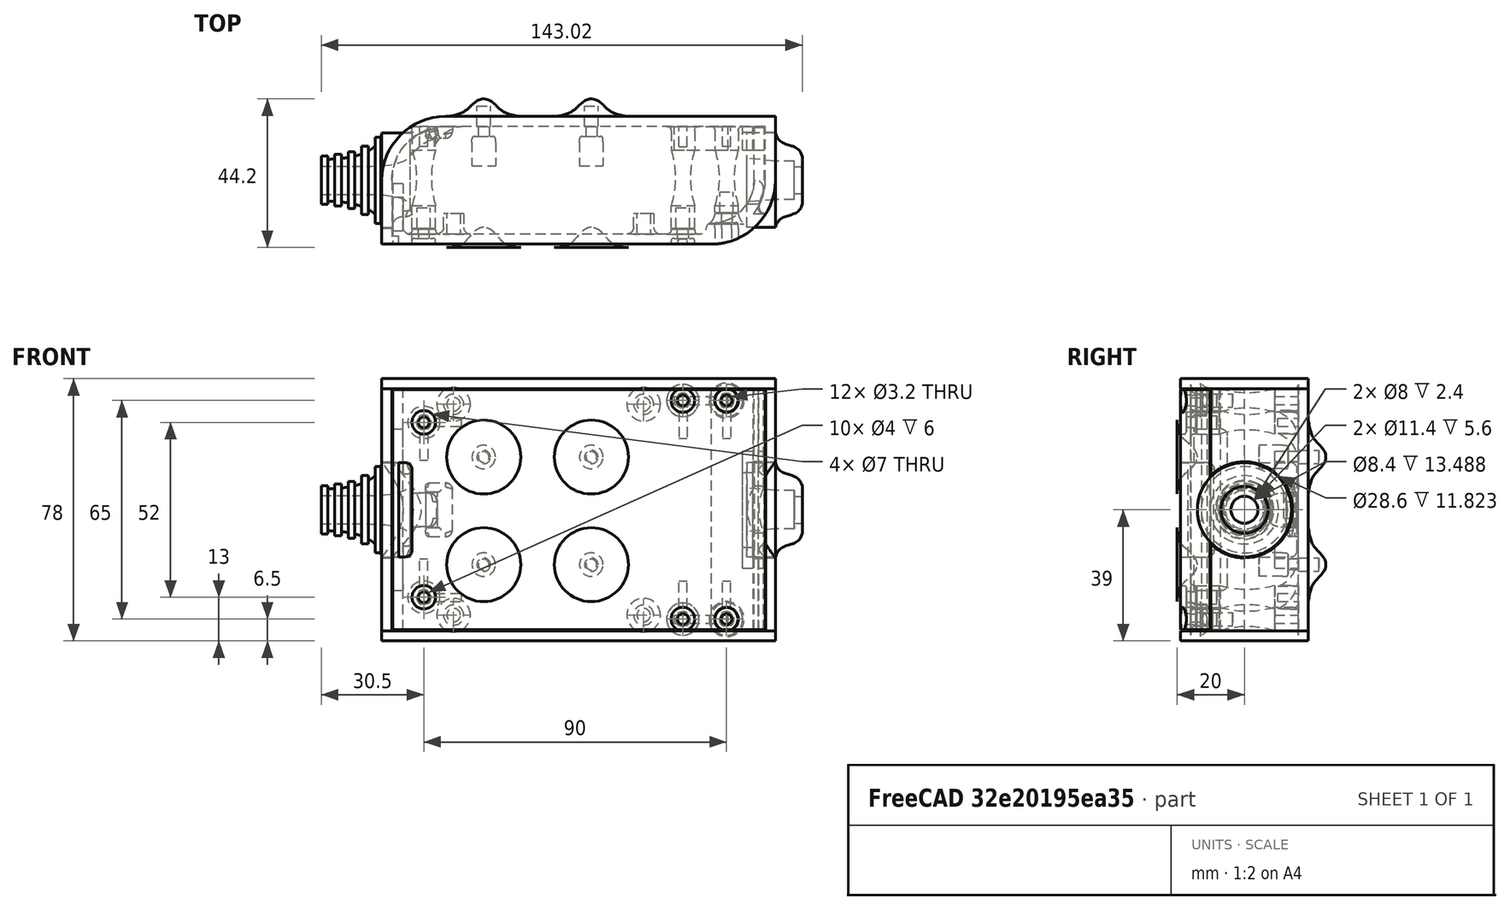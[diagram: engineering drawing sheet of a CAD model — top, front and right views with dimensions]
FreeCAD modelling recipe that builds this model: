
FCSTD DOCUMENT  (FreeCAD 0.19R0.19.2)
Label: enclosure_089
License: All rights reserved
LicenseURL: http://en.wikipedia.org/wiki/All_rights_reserved
objects: Part::Feature×68, Part::Revolution×68, Part::MultiFuse×50, Sketcher::SketchObject×28, Part::Fillet×22, Part::Cylinder×22, Part::Extrusion×18, Part::Cut×17, Part::Box×12, App::MeasureDistance×3
note: 305 computed .brp shape members not serialized (recipe doc carries the construction recipe); baked Part::Feature solids carry a one-line shape summary decoded from their .brp

FEATURE [Sketcher::SketchObject] Sketch  label="topSketch"
  FullyConstrained = true
  sketch-geometry (13):
    g0: LineSegment StartX=117 StartY=19 StartZ=0 EndX=117 EndY=38 EndZ=0
    g1: ArcOfCircle CenterX=98 CenterY=19 CenterZ=0 NormalX=0 NormalY=0 NormalZ=1 AngleXU=0 Radius=19 StartAngle=5.7297 EndAngle=6.28319
    g2: LineSegment StartX=0 StartY=3 StartZ=0 EndX=0 EndY=19 EndZ=0
    g3: LineSegment StartX=19 StartY=38 StartZ=0 EndX=117 EndY=38 EndZ=0
    g4: ArcOfCircle CenterX=19 CenterY=19 CenterZ=0 NormalX=0 NormalY=0 NormalZ=1 AngleXU=0 Radius=19 StartAngle=1.5708 EndAngle=3.14159
    g5: ArcOfCircle CenterX=19 CenterY=19 CenterZ=0 NormalX=0 NormalY=0 NormalZ=1 AngleXU=0 Radius=16 StartAngle=1.5708 EndAngle=3.14159
    g6: ArcOfCircle CenterX=98 CenterY=19 CenterZ=0 NormalX=0 NormalY=0 NormalZ=1 AngleXU=0 Radius=16 StartAngle=5.60905 EndAngle=6.28319
    g7: LineSegment StartX=114 StartY=19 StartZ=0 EndX=114 EndY=35 EndZ=0
    g8: LineSegment StartX=110.5 StartY=9.01251 StartZ=0 EndX=114.163 EndY=9.01251 EndZ=0
    g9: LineSegment StartX=114 StartY=35 StartZ=0 EndX=19 EndY=35 EndZ=0
    g10: LineSegment StartX=0 StartY=3 StartZ=0 EndX=0 EndY=0 EndZ=0
    g11: LineSegment StartX=3 StartY=0 StartZ=0 EndX=0 EndY=0 EndZ=0
    g12: LineSegment StartX=3 StartY=19 StartZ=0 EndX=3 EndY=0 EndZ=0
  constraints (33):
    c: Vertical(g0)
    c: Distance(g0) = 19
    c: Block(g0)
    c: Coincident(g1,g0)
    c: Block(g1)
    c: Vertical(g2)
    c: Block(g2)
    c: Coincident(g3,g0)
    c: Horizontal(g3)
    c: Distance(g3) = 98
    c: Coincident(g4,g3)
    c: Coincident(g4,g2)
    c: Block(g4)
    c: Coincident(g5,g4)
    c: Coincident(g6,g1)
    c: Block(g6)
    c: Block(g5)
    c: Coincident(g7,g6)
    c: Vertical(g7)
    c: Coincident(g8,g6)
    c: Coincident(g8,g1)
    c: Coincident(g9,g7)
    c: Coincident(g9,g5)
    c: Horizontal(g9)
    c: Tangent(g9,g5)
    c: Coincident(g10,g2)
    c: Distance(g10) = 3
    c: Vertical(g10)
    c: Coincident(g11,g10)
    c: Horizontal(g11)
    c: Coincident(g12,g5)
    c: Coincident(g12,g11)
    c: Vertical(g12)
FEATURE [Sketcher::SketchObject] Sketch001  label="bottomSketch"
  FullyConstrained = true
  sketch-geometry (32):
    g0: LineSegment StartX=3.3 StartY=-6.03275e-07 StartZ=0 EndX=98 EndY=-6.03275e-07 EndZ=0
    g1: ArcOfCircle CenterX=98 CenterY=19 CenterZ=0 NormalX=0 NormalY=0 NormalZ=1 AngleXU=0 Radius=19 StartAngle=4.71239 EndAngle=5.71103
    g2: LineSegment StartX=6.3 StartY=8 StartZ=0 EndX=3.3 EndY=8 EndZ=0
    g3: LineSegment StartX=3.3 StartY=8 StartZ=0 EndX=3.3 EndY=-6.03275e-07 EndZ=0
    g4: ArcOfCircle CenterX=8.3 CenterY=5 CenterZ=0 NormalX=0 NormalY=0 NormalZ=1 AngleXU=0 Radius=2 StartAngle=3.14159 EndAngle=4.71239
    g5: LineSegment StartX=6.3 StartY=8 StartZ=0 EndX=6.3 EndY=5 EndZ=0
    g6: ArcOfCircle CenterX=98 CenterY=19 CenterZ=0 NormalX=0 NormalY=0 NormalZ=1 AngleXU=0 Radius=12.7 StartAngle=4.71239 EndAngle=6.28319
    g7: LineSegment StartX=94.7 StartY=3 StartZ=0 EndX=8.3 EndY=3 EndZ=0
    g8-g12: Circle x5 (B-spline internal-alignment scaffolding for g13; pole/knot coordinates omitted)
    g13: BSplineCurve PolesCount=5 KnotsCount=3 Degree=3 IsPeriodic=0
    g14: GeomPoint X=98 Y=6.3 Z=0
    g15: GeomPoint X=96.3938 Y=4.71946 Z=0
    g16: GeomPoint X=94.7 Y=3 Z=0
    g17-g23: Circle x7 (B-spline internal-alignment scaffolding for g24; pole/knot coordinates omitted)
    g24: BSplineCurve PolesCount=7 KnotsCount=5 Degree=3 IsPeriodic=0
    g25-g29: GeomPoint x5 (B-spline internal-alignment scaffolding for g24; pole/knot coordinates omitted)
    g30: ArcOfCircle CenterX=98 CenterY=19 CenterZ=0 NormalX=0 NormalY=0 NormalZ=1 AngleXU=0 Radius=15.7 StartAngle=5.81226 EndAngle=6.28319
    g31: LineSegment StartX=110.7 StartY=19 StartZ=0 EndX=113.7 EndY=19 EndZ=0
  constraints (41):
    c: Horizontal(g0)
    c: Coincident(g1,g0)
    c: Block(g1)
    c: Horizontal(g2)
    c: Distance(g2) = 3
    c: Coincident(g3,g2)
    c: Vertical(g3)
    c: Coincident(g3,g0)
    c: Block(g4)
    c: Block(g2)
    c: Coincident(g5,g2)
    c: Coincident(g5,g4)
    c: Vertical(g5)
    c: Coincident(g6,g1)
    c: Block(g6)
    c: Coincident(g7,g4)
    c: Horizontal(g7)
    c: Block(g0)
    c: Block(g7)
    c: Block(g3)
    c: Coincident(g13,g6)
    c: Weight(g8) = 1
    c: Equal(g8, g9-g12) x4
    c: Coincident(g13,g7)
    c: InternalAlignment(g8-g12 -> g13) x5
    c: InternalAlignment(g14,g13)
    c: InternalAlignment(g15,g13)
    c: InternalAlignment(g16,g13)
    c: Block(g13)
    c: Weight(g17) = 1
    c: Equal(g17, g18-g23) x6
    c: Coincident(g24,g1)
    c: InternalAlignment(g17-g23 -> g24) x7
    c: InternalAlignment(g25-g29 -> g24) x5
    c: Block(g24)
    c: Coincident(g30,g24)
    c: Coincident(g31,g6)
    c: Coincident(g31,g30)
    c: Horizontal(g31)
    c: Block(g31)
    c: Block(g30)
FEATURE [Part::Extrusion] Extrude  label="top"
  Base = -> Sketch
  Dir = (0,0,1)
  DirMode = 2
  FaceMakerClass = Part::FaceMakerBullseye
  LengthFwd = 72
  LengthRev = 0
  Solid = true
  Symmetric = false
FEATURE [Part::Extrusion] Extrude001  label="bottom"
  Base = -> Sketch001
  Dir = (0,0,1)
  DirMode = 2
  FaceMakerClass = Part::FaceMakerBullseye
  LengthFwd = 71.4
  LengthRev = 0
  Placement = pos=(0,0,0.3) rot=(0,0,1;0rad)
  Solid = true
  Symmetric = false
FEATURE [Sketcher::SketchObject] Sketch002  label="topSketch001"
  FullyConstrained = true
  sketch-geometry (6):
    g0: LineSegment StartX=19 StartY=38 StartZ=0 EndX=117 EndY=38 EndZ=0
    g1: ArcOfCircle CenterX=19 CenterY=19 CenterZ=0 NormalX=0 NormalY=0 NormalZ=1 AngleXU=0 Radius=19 StartAngle=1.5708 EndAngle=3.14159
    g2: LineSegment StartX=117 StartY=38 StartZ=0 EndX=117 EndY=19 EndZ=0
    g3: LineSegment StartX=98 StartY=1.0161e-12 StartZ=0 EndX=5.22862e-06 EndY=1.0161e-12 EndZ=0
    g4: LineSegment StartX=5.22862e-06 StartY=19 StartZ=0 EndX=5.22862e-06 EndY=1.0161e-12 EndZ=0
    g5: ArcOfCircle CenterX=98 CenterY=19 CenterZ=0 NormalX=0 NormalY=0 NormalZ=1 AngleXU=0 Radius=19 StartAngle=4.71239 EndAngle=6.28319
  constraints (16):
    c: Horizontal(g0)
    c: Distance(g0) = 98
    c: Coincident(g1,g0)
    c: Block(g1)
    c: Coincident(g2,g0)
    c: Vertical(g2)
    c: Distance(g2) = 19
    c: Horizontal(g3)
    c: Coincident(g4,g1)
    c: Vertical(g4)
    c: Coincident(g3,g4)
    c: Block(g3)
    c: Coincident(g5,g2)
    c: Coincident(g5,g3)
    c: Block(g0)
    c: Block(g5)
FEATURE [Part::Extrusion] Extrude002  label="sideA"
  Base = -> Sketch002
  Dir = (0,0,1)
  DirMode = 2
  FaceMakerClass = Part::FaceMakerBullseye
  LengthFwd = 3
  LengthRev = 0
  Placement = pos=(0,0,-3) rot=(0,0,1;0rad)
  Solid = true
  Symmetric = false
FEATURE [Sketcher::SketchObject] Sketch003  label="topSketch002"
  FullyConstrained = true
  sketch-geometry (6):
    g0: LineSegment StartX=19 StartY=38 StartZ=0 EndX=117 EndY=38 EndZ=0
    g1: ArcOfCircle CenterX=19 CenterY=19 CenterZ=0 NormalX=0 NormalY=0 NormalZ=1 AngleXU=0 Radius=19 StartAngle=1.5708 EndAngle=3.14159
    g2: LineSegment StartX=117 StartY=38 StartZ=0 EndX=117 EndY=19 EndZ=0
    g3: LineSegment StartX=98 StartY=1.0161e-12 StartZ=0 EndX=5.22862e-06 EndY=1.0161e-12 EndZ=0
    g4: LineSegment StartX=5.22862e-06 StartY=19 StartZ=0 EndX=5.22862e-06 EndY=1.0161e-12 EndZ=0
    g5: ArcOfCircle CenterX=98 CenterY=19 CenterZ=0 NormalX=0 NormalY=0 NormalZ=1 AngleXU=0 Radius=19 StartAngle=4.71239 EndAngle=6.28319
  constraints (16):
    c: Horizontal(g0)
    c: Distance(g0) = 98
    c: Coincident(g1,g0)
    c: Block(g1)
    c: Coincident(g2,g0)
    c: Vertical(g2)
    c: Distance(g2) = 19
    c: Horizontal(g3)
    c: Coincident(g4,g1)
    c: Vertical(g4)
    c: Coincident(g3,g4)
    c: Block(g3)
    c: Coincident(g5,g2)
    c: Coincident(g5,g3)
    c: Block(g0)
    c: Block(g5)
FEATURE [Part::Extrusion] Extrude003  label="sideB"
  Base = -> Sketch003
  Dir = (0,0,1)
  DirMode = 2
  FaceMakerClass = Part::FaceMakerBullseye
  LengthFwd = 3
  LengthRev = 0
  Placement = pos=(0,0,72) rot=(0,0,1;0rad)
  Solid = true
  Symmetric = false
FEATURE [Sketcher::SketchObject] Sketch004
  FullyConstrained = true
  MapMode = 3
  Placement = pos=(0,0,0) rot=(1,0,0;1.5708rad)
  Support = -> [Extrude]
  sketch-geometry (8):
    g0: Circle CenterX=80.351 CenterY=-67.6202 CenterZ=0 NormalX=0 NormalY=0 NormalZ=1 AngleXU=0 Radius=2
    g1: Circle CenterX=80.351 CenterY=-67.6202 CenterZ=0 NormalX=0 NormalY=0 NormalZ=1 AngleXU=0 Radius=3
    g2: Circle CenterX=80.351 CenterY=-4.92017 CenterZ=0 NormalX=0 NormalY=0 NormalZ=1 AngleXU=0 Radius=2
    g3: Circle CenterX=80.351 CenterY=-4.92017 CenterZ=0 NormalX=0 NormalY=0 NormalZ=1 AngleXU=0 Radius=3
    g4: Circle CenterX=23.851 CenterY=-4.92017 CenterZ=0 NormalX=0 NormalY=0 NormalZ=1 AngleXU=0 Radius=2
    g5: Circle CenterX=23.851 CenterY=-4.92017 CenterZ=0 NormalX=0 NormalY=0 NormalZ=1 AngleXU=0 Radius=3
    g6: Circle CenterX=23.851 CenterY=-67.6202 CenterZ=0 NormalX=0 NormalY=0 NormalZ=1 AngleXU=0 Radius=2
    g7: Circle CenterX=23.851 CenterY=-67.6202 CenterZ=0 NormalX=0 NormalY=0 NormalZ=1 AngleXU=0 Radius=3
  constraints (8):
    c: Block(g3)
    c: Block(g2)
    c: Block(g1)
    c: Block(g0)
    c: Block(g6)
    c: Block(g7)
    c: Block(g4)
    c: Block(g5)
FEATURE [Part::Extrusion] Extrude004
  Base = -> Sketch004
  Dir = (0,-1,2e-16)
  DirMode = 2
  FaceMakerClass = Part::FaceMakerBullseye
  LengthFwd = 6
  LengthRev = 0
  Placement = pos=(0,9,0) rot=(0,0,1;0rad)
  Solid = true
  Symmetric = false
FEATURE [Sketcher::SketchObject] Sketch005
  FullyConstrained = true
  MapMode = 3
  Placement = pos=(0,0,0) rot=(1,0,0;1.5708rad)
  Support = -> [Extrude]
  sketch-geometry (8):
    g0: Circle CenterX=80.351 CenterY=-67.6202 CenterZ=0 NormalX=0 NormalY=0 NormalZ=1 AngleXU=0 Radius=3
    g1: Circle CenterX=80.351 CenterY=-4.92017 CenterZ=0 NormalX=0 NormalY=0 NormalZ=1 AngleXU=0 Radius=3
    g2: Circle CenterX=23.851 CenterY=-4.92017 CenterZ=0 NormalX=0 NormalY=0 NormalZ=1 AngleXU=0 Radius=3
    g3: Circle CenterX=23.851 CenterY=-67.6202 CenterZ=0 NormalX=0 NormalY=0 NormalZ=1 AngleXU=0 Radius=3
    g4: Circle CenterX=23.851 CenterY=-67.6202 CenterZ=0 NormalX=0 NormalY=0 NormalZ=1 AngleXU=0 Radius=5
    g5: Circle CenterX=80.351 CenterY=-67.6202 CenterZ=0 NormalX=0 NormalY=0 NormalZ=1 AngleXU=0 Radius=5
    g6: Circle CenterX=23.851 CenterY=-4.92017 CenterZ=0 NormalX=0 NormalY=0 NormalZ=1 AngleXU=0 Radius=5
    g7: Circle CenterX=80.351 CenterY=-4.92017 CenterZ=0 NormalX=0 NormalY=0 NormalZ=1 AngleXU=0 Radius=5
  constraints (8):
    c: Block(g1)
    c: Block(g0)
    c: Block(g3)
    c: Block(g2)
    c: Block(g5)
    c: Block(g4)
    c: Block(g6)
    c: Block(g7)
FEATURE [Part::Extrusion] Extrude005
  Base = -> Sketch005
  Dir = (0,-1,2e-16)
  DirMode = 2
  FaceMakerClass = Part::FaceMakerBullseye
  LengthFwd = 2
  LengthRev = 0
  Solid = true
  Symmetric = false
FEATURE [Sketcher::SketchObject] Sketch006
  FullyConstrained = true
  MapMode = 3
  Placement = pos=(0,0,0) rot=(1,0,0;1.5708rad)
  sketch-geometry (8):
    g0: Circle CenterX=80.351 CenterY=-67.6202 CenterZ=0 NormalX=0 NormalY=0 NormalZ=1 AngleXU=0 Radius=3
    g1: Circle CenterX=80.351 CenterY=-4.92017 CenterZ=0 NormalX=0 NormalY=0 NormalZ=1 AngleXU=0 Radius=3
    g2: Circle CenterX=23.851 CenterY=-4.92017 CenterZ=0 NormalX=0 NormalY=0 NormalZ=1 AngleXU=0 Radius=3
    g3: Circle CenterX=23.851 CenterY=-67.6202 CenterZ=0 NormalX=0 NormalY=0 NormalZ=1 AngleXU=0 Radius=3
    g4: Circle CenterX=23.851 CenterY=-67.6202 CenterZ=0 NormalX=0 NormalY=0 NormalZ=1 AngleXU=0 Radius=5
    g5: Circle CenterX=80.351 CenterY=-67.6202 CenterZ=0 NormalX=0 NormalY=0 NormalZ=1 AngleXU=0 Radius=5
    g6: Circle CenterX=23.851 CenterY=-4.92017 CenterZ=0 NormalX=0 NormalY=0 NormalZ=1 AngleXU=0 Radius=5
    g7: Circle CenterX=80.351 CenterY=-4.92017 CenterZ=0 NormalX=0 NormalY=0 NormalZ=1 AngleXU=0 Radius=5
  constraints (8):
    c: Block(g1)
    c: Block(g0)
    c: Block(g3)
    c: Block(g2)
    c: Block(g5)
    c: Block(g4)
    c: Block(g6)
    c: Block(g7)
FEATURE [Part::Extrusion] Extrude007
  Base = -> Sketch006
  Dir = (0,-1,2e-16)
  DirMode = 2
  FaceMakerClass = Part::FaceMakerBullseye
  LengthFwd = 2
  LengthRev = 0
  Solid = true
  Symmetric = false
FEATURE [Part::Fillet] Fillet
  Base = -> Extrude007
  Edges = 4 edges r=1.99: [Edge6,Edge12,Edge18,Edge24]
FEATURE [Part::Cut] Cut
  Base = -> Extrude005
  Placement = pos=(0,5,0) rot=(0,0,1;0rad)
  Tool = -> Fillet
FEATURE [Part::MultiFuse] Fusion  label="pCBScrews"
  Placement = pos=(-2.5,0,72.3) rot=(0,0,1;0rad)
  Shapes = -> [Extrude004,Cut]
FEATURE [App::MeasureDistance] Distance  label="Distance: 0.69 mm"
  Distance = 0.685967
  P1 = (24.0138,2.9647,0.3)
  P2 = (23.8901,3,-0.373787)
FEATURE [App::MeasureDistance] Distance001  label="Distance: 0.53 mm"
  Distance = 0.533607
  P1 = (80.2939,3,72.2334)
  P2 = (80.281,2.99661,71.7)
FEATURE [Part::Fillet] Fillet001
  Base = -> Extrude001
  Edges = 1 edges r=2.4: [Edge17]
FEATURE [Part::Fillet] Fillet002  label="bottom001"
  Base = -> Fillet001
  Edges = 1 edges r=2.4: [Edge36]
FEATURE [Part::Fillet] Fillet003  label="top001"
  Base = -> Extrude
  Edges = 1 edges r=2: [Edge1]
FEATURE [Sketcher::SketchObject] Sketch007
  FullyConstrained = true
  sketch-geometry (16):
    g0: LineSegment StartX=4 StartY=0 StartZ=0 EndX=4 EndY=2.4 EndZ=0
    g1: LineSegment StartX=4 StartY=2.4 StartZ=0 EndX=7 EndY=2.4 EndZ=0
    g2: LineSegment StartX=4 StartY=0 StartZ=0 EndX=5.7 EndY=0 EndZ=0
    g3: LineSegment StartX=5.7 StartY=0 StartZ=0 EndX=5.7 EndY=-5.6 EndZ=0
    g4-g8: Circle x5 (B-spline internal-alignment scaffolding for g9; pole/knot coordinates omitted)
    g9: BSplineCurve PolesCount=5 KnotsCount=3 Degree=3 IsPeriodic=0
    g10: GeomPoint X=7 Y=2.4 Z=0
    g11: GeomPoint X=10.4582 Y=-1.55472 Z=0
    g12: GeomPoint X=14 Y=-5.6 Z=0
    g13: LineSegment StartX=14 StartY=-5.6 StartZ=0 EndX=14 EndY=-14.1 EndZ=0
    g14: LineSegment StartX=14 StartY=-14.1 StartZ=0 EndX=6.5 EndY=-14.1 EndZ=0
    g15: LineSegment StartX=5.7 StartY=-5.6 StartZ=0 EndX=6.5 EndY=-14.1 EndZ=0
  constraints (28):
    c: Distance(g0) = 2.4
    c: Vertical(g0)
    c: Block(g0)
    c: Coincident(g1,g0)
    c: Horizontal(g1)
    c: Distance(g1) = 3
    c: Coincident(g2,g0)
    c: Horizontal(g2)
    c: Distance(g2) = 1.7
    c: Coincident(g3,g2)
    c: Vertical(g3)
    c: Distance(g3) = 5.6
    c: Coincident(g9,g1)
    c: Weight(g4) = 1
    c: Equal(g4, g5-g8) x4
    c: InternalAlignment(g4-g8 -> g9) x5
    c: InternalAlignment(g10,g9)
    c: InternalAlignment(g11,g9)
    c: InternalAlignment(g12,g9)
    c: Block(g9)
    c: Coincident(g13,g9)
    c: Vertical(g13)
    c: Distance(g13) = 8.5
    c: Coincident(g14,g13)
    c: Horizontal(g14)
    c: Distance(g14) = 7.5
    c: Coincident(g15,g3)
    c: Coincident(g15,g14)
FEATURE [Part::Feature] Face
  shape: bbox 10 x 16.5 x 2e-07 mm, 1 faces, 0 solids (baked)
FEATURE [Part::Revolution] Revolve  label="plugHousing"
  Angle = 360
  Axis = (0,1,0)
  Base = (0,0,0)
  FaceMakerClass = Part::FaceMakerBullseye
  Placement = pos=(0,0,36.15) rot=(0,0,1;0rad)
  Solid = false
  Source = -> Face
  Symmetric = false
FEATURE [Part::Feature] Face001
  shape: bbox 10 x 16.5 x 2e-07 mm, 1 faces, 0 solids (baked)
FEATURE [Part::Revolution] Revolve001  label="plugHousing001"
  Angle = 360
  Axis = (0,1,0)
  Base = (0,0,0)
  FaceMakerClass = Part::FaceMakerBullseye
  Placement = pos=(0,0,36.15) rot=(0,0,1;0rad)
  Solid = false
  Source = -> Face001
  Symmetric = false
FEATURE [Part::MultiFuse] Fusion001  label="plugHousing002"
  Placement = pos=(0,0,0) rot=(0,0,1;1.5708rad)
  Shapes = -> [Revolve001,Revolve]
FEATURE [Part::Feature] Face002
  shape: bbox 10 x 16.5 x 2e-07 mm, 1 faces, 0 solids (baked)
FEATURE [Part::Revolution] Revolve003  label="plugHousing005"
  Angle = 360
  Axis = (0,1,0)
  Base = (0,0,0)
  FaceMakerClass = Part::FaceMakerBullseye
  Placement = pos=(0,0,36.15) rot=(0,0,1;0rad)
  Solid = false
  Source = -> Face002
  Symmetric = false
FEATURE [Part::Feature] Face003
  shape: bbox 10 x 16.5 x 2e-07 mm, 1 faces, 0 solids (baked)
FEATURE [Part::Revolution] Revolve002  label="plugHousing003"
  Angle = 360
  Axis = (0,1,0)
  Base = (0,0,0)
  FaceMakerClass = Part::FaceMakerBullseye
  Placement = pos=(0,0,36.15) rot=(0,0,1;0rad)
  Solid = false
  Source = -> Face003
  Symmetric = false
FEATURE [Part::MultiFuse] Fusion002  label="plugHousing004"
  Placement = pos=(0,0,0) rot=(0,0,1;1.5708rad)
  Shapes = -> [Revolve002,Revolve003]
FEATURE [Part::MultiFuse] Fusion003  label="plugHousing006"
  Placement = pos=(0,19,0) rot=(0,0,1;3.14159rad)
  Shapes = -> [Fusion002,Fusion001]
FEATURE [Part::Feature] Face004
  shape: bbox 10 x 16.5 x 2e-07 mm, 1 faces, 0 solids (baked)
FEATURE [Part::Revolution] Revolve006  label="plugHousing010"
  Angle = 360
  Axis = (0,1,0)
  Base = (0,0,0)
  FaceMakerClass = Part::FaceMakerBullseye
  Placement = pos=(0,0,36.15) rot=(0,0,1;0rad)
  Solid = false
  Source = -> Face004
  Symmetric = false
FEATURE [Part::Feature] Face005
  shape: bbox 10 x 16.5 x 2e-07 mm, 1 faces, 0 solids (baked)
FEATURE [Part::Revolution] Revolve007  label="plugHousing011"
  Angle = 360
  Axis = (0,1,0)
  Base = (0,0,0)
  FaceMakerClass = Part::FaceMakerBullseye
  Placement = pos=(0,0,36.15) rot=(0,0,1;0rad)
  Solid = false
  Source = -> Face005
  Symmetric = false
FEATURE [Part::Feature] Face006
  shape: bbox 10 x 16.5 x 2e-07 mm, 1 faces, 0 solids (baked)
FEATURE [Part::Revolution] Revolve004  label="plugHousing007"
  Angle = 360
  Axis = (0,1,0)
  Base = (0,0,0)
  FaceMakerClass = Part::FaceMakerBullseye
  Placement = pos=(0,0,36.15) rot=(0,0,1;0rad)
  Solid = false
  Source = -> Face006
  Symmetric = false
FEATURE [Part::MultiFuse] Fusion004  label="plugHousing009"
  Placement = pos=(0,0,0) rot=(0,0,1;1.5708rad)
  Shapes = -> [Revolve004,Revolve007]
FEATURE [Part::Feature] Face007
  shape: bbox 10 x 16.5 x 2e-07 mm, 1 faces, 0 solids (baked)
FEATURE [Part::Revolution] Revolve005  label="plugHousing008"
  Angle = 360
  Axis = (0,1,0)
  Base = (0,0,0)
  FaceMakerClass = Part::FaceMakerBullseye
  Placement = pos=(0,0,36.15) rot=(0,0,1;0rad)
  Solid = false
  Source = -> Face007
  Symmetric = false
FEATURE [Part::MultiFuse] Fusion005  label="plugHousing012"
  Placement = pos=(0,0,0) rot=(0,0,1;1.5708rad)
  Shapes = -> [Revolve006,Revolve005]
FEATURE [Part::MultiFuse] Fusion006  label="plugHousing013"
  Placement = pos=(0,19,0) rot=(0,0,1;3.14159rad)
  Shapes = -> [Fusion005,Fusion004]
FEATURE [Part::MultiFuse] Fusion007  label="plugHousing014"
  Placement = pos=(122.621,0,-0.15) rot=(0,0,1;0rad)
  Shapes = -> [Fusion003,Fusion006]
FEATURE [Part::Cylinder] Cylinder002
  Angle = 360
  AttacherType = Attacher::AttachEngine3D
  Height = 20
  Placement = pos=(0,0,36.15) rot=(0,0,1;0rad)
  Radius = 4
FEATURE [Part::Cylinder] Cylinder003
  Angle = 360
  AttacherType = Attacher::AttachEngine3D
  Height = 10
  Placement = pos=(0,0,36.15) rot=(0,0,1;0rad)
  Radius = 4
FEATURE [Part::MultiFuse] Fusion009  label="removeToCreateHoleForPlugHousing"
  Placement = pos=(70,19,36.15) rot=(0,1,0;1.5708rad)
  Shapes = -> [Cylinder002,Cylinder003]
FEATURE [Part::Cylinder] Cylinder004
  Angle = 360
  AttacherType = Attacher::AttachEngine3D
  Height = 20
  Placement = pos=(0,0,36.15) rot=(0,0,1;0rad)
  Radius = 4
FEATURE [Part::Cylinder] Cylinder005
  Angle = 360
  AttacherType = Attacher::AttachEngine3D
  Height = 10
  Placement = pos=(0,0,36.15) rot=(0,0,1;0rad)
  Radius = 4
FEATURE [Part::MultiFuse] Fusion010  label="removeToCreateHoleForPlugHousing001"
  Placement = pos=(70,19,36.15) rot=(0,1,0;1.5708rad)
  Shapes = -> [Cylinder004,Cylinder005]
FEATURE [Part::Cut] Cut001
  Base = -> Fillet003
  Tool = -> Fusion010
FEATURE [Part::Cut] Cut002  label="Bottom"
  Base = -> Fillet002
  Tool = -> Fusion009
FEATURE [Part::Feature] Face008
  shape: bbox 10 x 16.5 x 2e-07 mm, 1 faces, 0 solids (baked)
FEATURE [Part::Revolution] Revolve011  label="plugHousing021"
  Angle = 360
  Axis = (0,1,0)
  Base = (0,0,0)
  FaceMakerClass = Part::FaceMakerBullseye
  Placement = pos=(0,0,36.15) rot=(0,0,1;0rad)
  Solid = false
  Source = -> Face008
  Symmetric = false
FEATURE [Part::Feature] Face009
  shape: bbox 10 x 16.5 x 2e-07 mm, 1 faces, 0 solids (baked)
FEATURE [Part::Revolution] Revolve012  label="plugHousing022"
  Angle = 360
  Axis = (0,1,0)
  Base = (0,0,0)
  FaceMakerClass = Part::FaceMakerBullseye
  Placement = pos=(0,0,36.15) rot=(0,0,1;0rad)
  Solid = false
  Source = -> Face009
  Symmetric = false
FEATURE [Part::Feature] Face010 .. Face013  x4 (patterned run collapsed; names and placements below)
  shape: bbox 10 x 16.5 x 2e-07 mm, 1 faces, 0 solids (baked)
FEATURE [Part::Revolution] Revolve015  label="plugHousing027"
  Angle = 360
  Axis = (0,1,0)
  Base = (0,0,0)
  FaceMakerClass = Part::FaceMakerBullseye
  Placement = pos=(0,0,36.15) rot=(0,0,1;0rad)
  Solid = false
  Source = -> Face013
  Symmetric = false
FEATURE [Part::Feature] Face014
  shape: bbox 10 x 16.5 x 2e-07 mm, 1 faces, 0 solids (baked)
FEATURE [Part::Feature] Face015
  shape: bbox 10 x 16.5 x 2e-07 mm, 1 faces, 0 solids (baked)
FEATURE [Part::Feature] Face016
  shape: bbox 10 x 16.5 x 2e-07 mm, 1 faces, 0 solids (baked)
FEATURE [Part::Revolution] Revolve019  label="plugHousing033"
  Angle = 360
  Axis = (0,1,0)
  Base = (0,0,0)
  FaceMakerClass = Part::FaceMakerBullseye
  Placement = pos=(0,0,36.15) rot=(0,0,1;0rad)
  Solid = false
  Source = -> Face016
  Symmetric = false
FEATURE [Part::Feature] Face017
  shape: bbox 10 x 16.5 x 2e-07 mm, 1 faces, 0 solids (baked)
FEATURE [Part::Revolution] Revolve020  label="plugHousing034"
  Angle = 360
  Axis = (0,1,0)
  Base = (0,0,0)
  FaceMakerClass = Part::FaceMakerBullseye
  Placement = pos=(0,0,36.15) rot=(0,0,1;0rad)
  Solid = false
  Source = -> Face017
  Symmetric = false
FEATURE [Part::Feature] Face018
  shape: bbox 10 x 16.5 x 2e-07 mm, 1 faces, 0 solids (baked)
FEATURE [Part::Revolution] Revolve016  label="plugHousing030"
  Angle = 360
  Axis = (0,1,0)
  Base = (0,0,0)
  FaceMakerClass = Part::FaceMakerBullseye
  Placement = pos=(0,0,36.15) rot=(0,0,1;0rad)
  Solid = false
  Source = -> Face018
  Symmetric = false
FEATURE [Part::MultiFuse] Fusion020  label="plugHousing038"
  Placement = pos=(0,0,0) rot=(0,0,1;1.5708rad)
  Shapes = -> [Revolve016,Revolve020]
FEATURE [Part::Feature] Face019
  shape: bbox 10 x 16.5 x 2e-07 mm, 1 faces, 0 solids (baked)
FEATURE [Part::Feature] Face020
  shape: bbox 10 x 16.5 x 2e-07 mm, 1 faces, 0 solids (baked)
FEATURE [Part::Revolution] Revolve017  label="plugHousing031"
  Angle = 360
  Axis = (0,1,0)
  Base = (0,0,0)
  FaceMakerClass = Part::FaceMakerBullseye
  Placement = pos=(0,0,36.15) rot=(0,0,1;0rad)
  Solid = false
  Source = -> Face020
  Symmetric = false
FEATURE [Part::MultiFuse] Fusion021  label="plugHousing039"
  Placement = pos=(0,0,0) rot=(0,0,1;1.5708rad)
  Shapes = -> [Revolve019,Revolve017]
FEATURE [Part::MultiFuse] Fusion023  label="plugHousing041"
  Placement = pos=(0,19,0) rot=(0,0,1;3.14159rad)
  Shapes = -> [Fusion021,Fusion020]
FEATURE [Part::Revolution] Revolve022  label="plugHousing043"
  Angle = 360
  Axis = (0,1,0)
  Base = (0,0,0)
  FaceMakerClass = Part::FaceMakerBullseye
  Placement = pos=(0,0,36.15) rot=(0,0,1;0rad)
  Solid = false
  Source = -> Face019
  Symmetric = false
FEATURE [Part::Feature] Face021
  shape: bbox 10 x 16.5 x 2e-07 mm, 1 faces, 0 solids (baked)
FEATURE [Part::Revolution] Revolve023  label="plugHousing044"
  Angle = 360
  Axis = (0,1,0)
  Base = (0,0,0)
  FaceMakerClass = Part::FaceMakerBullseye
  Placement = pos=(0,0,36.15) rot=(0,0,1;0rad)
  Solid = false
  Source = -> Face021
  Symmetric = false
FEATURE [Part::Feature] Face022
  shape: bbox 10 x 16.5 x 2e-07 mm, 1 faces, 0 solids (baked)
FEATURE [Part::Revolution] Revolve018  label="plugHousing032"
  Angle = 360
  Axis = (0,1,0)
  Base = (0,0,0)
  FaceMakerClass = Part::FaceMakerBullseye
  Placement = pos=(0,0,36.15) rot=(0,0,1;0rad)
  Solid = false
  Source = -> Face022
  Symmetric = false
FEATURE [Part::MultiFuse] Fusion022  label="plugHousing040"
  Placement = pos=(0,0,0) rot=(0,0,1;1.5708rad)
  Shapes = -> [Revolve018,Revolve023]
FEATURE [Part::Feature] Face023
  shape: bbox 10 x 16.5 x 2e-07 mm, 1 faces, 0 solids (baked)
FEATURE [Part::Revolution] Revolve021  label="plugHousing035"
  Angle = 360
  Axis = (0,1,0)
  Base = (0,0,0)
  FaceMakerClass = Part::FaceMakerBullseye
  Placement = pos=(0,0,36.15) rot=(0,0,1;0rad)
  Solid = false
  Source = -> Face023
  Symmetric = false
FEATURE [Part::MultiFuse] Fusion018  label="plugHousing036"
  Placement = pos=(0,0,0) rot=(0,0,1;1.5708rad)
  Shapes = -> [Revolve022,Revolve021]
FEATURE [Part::MultiFuse] Fusion019  label="plugHousing037"
  Placement = pos=(0,19,0) rot=(0,0,1;3.14159rad)
  Shapes = -> [Fusion018,Fusion022]
FEATURE [Part::MultiFuse] Fusion024  label="plugHousing042"
  Placement = pos=(122.621,0,-0.15) rot=(0,0,1;0rad)
  Shapes = -> [Fusion023,Fusion019]
FEATURE [Part::Cylinder] Cylinder006
  Angle = 360
  AttacherType = Attacher::AttachEngine3D
  Height = 20
  Placement = pos=(0,0,36.15) rot=(0,0,1;0rad)
  Radius = 14.3
FEATURE [Part::Cylinder] Cylinder007
  Angle = 360
  AttacherType = Attacher::AttachEngine3D
  Height = 10
  Placement = pos=(0,0,36.15) rot=(0,0,1;0rad)
  Radius = 4
FEATURE [Part::MultiFuse] Fusion026  label="removeToCreteHoleForPlugHousing"
  Placement = pos=(70,19,36) rot=(0,1,0;1.5708rad)
  Shapes = -> [Cylinder006,Cylinder007]
FEATURE [Part::Box] Box001  label="Cube001"
  AttacherType = Attacher::AttachEngine3D
  Height = 28
  Length = 3
  Placement = pos=(110.7,19,22) rot=(0,0,1;0rad)
  Width = 15.7
FEATURE [Part::Cut] Cut003  label="top002"
  Base = -> Cut001
  Tool = -> Fusion007
FEATURE [Part::Revolution] Revolve008  label="plugHousing015"
  Angle = 360
  Axis = (0,1,0)
  Base = (0,0,0)
  FaceMakerClass = Part::FaceMakerBullseye
  Placement = pos=(0,0,36.15) rot=(0,0,1;0rad)
  Solid = false
  Source = -> Face010
  Symmetric = false
FEATURE [Part::MultiFuse] Fusion013  label="plugHousing020"
  Placement = pos=(0,0,0) rot=(0,0,1;1.5708rad)
  Shapes = -> [Revolve008,Revolve012]
FEATURE [Part::Cut] Cut004  label="top003"
  Base = -> Cut003
  Placement = pos=(1,0,0) rot=(0,0,1;0rad)
  Tool = -> Fusion026
FEATURE [Part::Cylinder] Cylinder008
  Angle = 360
  AttacherType = Attacher::AttachEngine3D
  Height = 20
  Placement = pos=(0,0,36.15) rot=(0,0,1;0rad)
  Radius = 10.3
FEATURE [Part::Cylinder] Cylinder009
  Angle = 360
  AttacherType = Attacher::AttachEngine3D
  Height = 10
  Placement = pos=(0,0,36.15) rot=(0,0,1;0rad)
  Radius = 4
FEATURE [Part::MultiFuse] Fusion027  label="removeToCreteHoleForPlugHousing001"
  Placement = pos=(70,19,36) rot=(0,1,0;1.5708rad)
  Shapes = -> [Cylinder008,Cylinder009]
FEATURE [Part::Cut] Cut005  label="plugHousingTab"
  Base = -> Box001
  Tool = -> Fusion027
FEATURE [Part::MultiFuse] Fusion028  label="plugHousing045"
  Shapes = -> [Fusion024,Cut005]
FEATURE [Part::Box] Box002  label="Cube002"
  AttacherType = Attacher::AttachEngine3D
  Height = 28.8
  Length = 3
  Placement = pos=(107.3,28,21.6) rot=(0,0,1;0rad)
  Width = 7
FEATURE [Part::Box] Box003  label="Cube003"
  AttacherType = Attacher::AttachEngine3D
  Height = 3
  Length = 6.4
  Placement = pos=(107.3,28,18.6) rot=(0,0,1;0rad)
  Width = 7
FEATURE [Part::Box] Box004  label="Cube004"
  AttacherType = Attacher::AttachEngine3D
  Height = 3
  Length = 6.4
  Placement = pos=(107.3,28,50.4) rot=(0,0,1;0rad)
  Width = 7
FEATURE [Part::MultiFuse] Fusion029  label="plugHousingBracketHolder"
  Shapes = -> [Box004,Box002,Box003]
FEATURE [Part::Cylinder] Cylinder010
  Angle = 360
  AttacherType = Attacher::AttachEngine3D
  Height = 20
  Placement = pos=(0,0,36.15) rot=(0,0,1;0rad)
  Radius = 14.3
FEATURE [Part::Cylinder] Cylinder011
  Angle = 360
  AttacherType = Attacher::AttachEngine3D
  Height = 10
  Placement = pos=(0,0,36.15) rot=(0,0,1;0rad)
  Radius = 4
FEATURE [Part::MultiFuse] Fusion030  label="removeToCreteHoleForPlugHousing002"
  Placement = pos=(70,19,36) rot=(0,1,0;1.5708rad)
  Shapes = -> [Cylinder010,Cylinder011]
FEATURE [Part::Cut] Cut006  label="plugHousingBracketHolder001"
  Base = -> Fusion029
  Tool = -> Fusion030
FEATURE [Part::Cylinder] Cylinder012
  Angle = 360
  AttacherType = Attacher::AttachEngine3D
  Height = 20
  Placement = pos=(0,0,36.15) rot=(0,0,1;0rad)
  Radius = 7
FEATURE [Part::Cylinder] Cylinder013
  Angle = 360
  AttacherType = Attacher::AttachEngine3D
  Height = 10
  Placement = pos=(0,0,36.15) rot=(0,0,1;0rad)
  Radius = 4
FEATURE [Part::MultiFuse] Fusion032  label="removeToCreteHoleForPlugHousing003"
  Placement = pos=(70,19,36) rot=(0,1,0;1.5708rad)
  Shapes = -> [Cylinder012,Cylinder013]
FEATURE [Part::Cut] Cut007  label="bottom002"
  Base = -> Cut002
  Tool = -> Fusion032
FEATURE [Sketcher::SketchObject] Sketch008
  FullyConstrained = true
  sketch-geometry (54):
    g0: LineSegment StartX=-4.2 StartY=0 StartZ=0 EndX=-6.2 EndY=0 EndZ=0
    g1: LineSegment StartX=-14 StartY=-18 StartZ=0 EndX=-14 EndY=-26.5 EndZ=0
    g2: LineSegment StartX=-4.2 StartY=0 StartZ=0 EndX=-4.2 EndY=-13.4877 EndZ=0
    g3: Circle CenterX=-4.2 CenterY=-13.4877 CenterZ=0 NormalX=0 NormalY=0 NormalZ=1 AngleXU=0 Radius=1
    g4: Circle CenterX=-4.2 CenterY=-26.5 CenterZ=0 NormalX=0 NormalY=0 NormalZ=1 AngleXU=0 Radius=1
    g5: Circle CenterX=-8.2 CenterY=-26.5 CenterZ=0 NormalX=0 NormalY=0 NormalZ=1 AngleXU=0 Radius=1
    g6: BSplineCurve PolesCount=3 KnotsCount=2 Degree=2 IsPeriodic=0
    g7: GeomPoint X=-4.2 Y=-13.4877 Z=0
    g8: GeomPoint X=-8.2 Y=-26.5 Z=0
    g9: LineSegment StartX=-14 StartY=-26.5 StartZ=0 EndX=-8.2 EndY=-26.5 EndZ=0
    g10: LineSegment StartX=-10.15 StartY=-12 StartZ=0 EndX=-10.15 EndY=-14 EndZ=0
    g11: LineSegment StartX=-12.8401 StartY=-16 StartZ=0 EndX=-10.1571 EndY=-16 EndZ=0
    g12: LineSegment StartX=-10.15 StartY=-14 StartZ=0 EndX=-8.70761 EndY=-14 EndZ=0
    g13: LineSegment StartX=-12.8401 StartY=-16 StartZ=0 EndX=-12.8401 EndY=-17.6958 EndZ=0
    g14: LineSegment StartX=-10.15 StartY=-12 StartZ=0 EndX=-7.79258 EndY=-12 EndZ=0
    g15: Circle CenterX=-6.2215 CenterY=-2 CenterZ=0 NormalX=0 NormalY=0 NormalZ=1 AngleXU=0 Radius=1
    g16: Circle CenterX=-6.22762 CenterY=-2.58724 CenterZ=0 NormalX=0 NormalY=0 NormalZ=1 AngleXU=0 Radius=1
    g17: Circle CenterX=-6.32538 CenterY=-4 CenterZ=0 NormalX=0 NormalY=0 NormalZ=1 AngleXU=0 Radius=1
    g18: BSplineCurve PolesCount=3 KnotsCount=2 Degree=2 IsPeriodic=0
    g19: GeomPoint X=-6.2215 Y=-2 Z=0
    g20: GeomPoint X=-6.32538 Y=-4 Z=0
    g21: Circle CenterX=-6.48644 CenterY=-5.99526 CenterZ=0 NormalX=0 NormalY=0 NormalZ=1 AngleXU=0 Radius=1
    g22: Circle CenterX=-6.58486 CenterY=-6.99526 CenterZ=0 NormalX=0 NormalY=0 NormalZ=1 AngleXU=0 Radius=1
    g23: Circle CenterX=-6.77343 CenterY=-8 CenterZ=0 NormalX=0 NormalY=0 NormalZ=1 AngleXU=0 Radius=1
    g24: BSplineCurve PolesCount=3 KnotsCount=2 Degree=2 IsPeriodic=0
    g25: GeomPoint X=-6.48644 Y=-5.99526 Z=0
    g26: GeomPoint X=-6.77343 Y=-8 Z=0
    g27: Circle CenterX=-7.19003 CenterY=-10 CenterZ=0 NormalX=0 NormalY=0 NormalZ=1 AngleXU=0 Radius=1
    g28: Circle CenterX=-7.44407 CenterY=-11.0915 CenterZ=0 NormalX=0 NormalY=0 NormalZ=1 AngleXU=0 Radius=1
    g29: Circle CenterX=-7.79258 CenterY=-12 CenterZ=0 NormalX=0 NormalY=0 NormalZ=1 AngleXU=0 Radius=1
    g30: BSplineCurve PolesCount=3 KnotsCount=2 Degree=2 IsPeriodic=0
    g31: GeomPoint X=-7.19003 Y=-10 Z=0
    g32: GeomPoint X=-7.79258 Y=-12 Z=0
    g33: Circle CenterX=-8.70761 CenterY=-14 CenterZ=0 NormalX=0 NormalY=0 NormalZ=1 AngleXU=0 Radius=1
    g34: Circle CenterX=-9.33087 CenterY=-15.1837 CenterZ=0 NormalX=0 NormalY=0 NormalZ=1 AngleXU=0 Radius=1
    g35: Circle CenterX=-10.1571 CenterY=-16 CenterZ=0 NormalX=0 NormalY=0 NormalZ=1 AngleXU=0 Radius=1
    g36: BSplineCurve PolesCount=3 KnotsCount=2 Degree=2 IsPeriodic=0
    g37: GeomPoint X=-8.70761 Y=-14 Z=0
    g38: GeomPoint X=-10.1571 Y=-16 Z=0
    g39: Circle CenterX=-12.8401 CenterY=-17.6958 CenterZ=0 NormalX=0 NormalY=0 NormalZ=1 AngleXU=0 Radius=1
    g40: Circle CenterX=-13.3521 CenterY=-17.9027 CenterZ=0 NormalX=0 NormalY=0 NormalZ=1 AngleXU=0 Radius=1
    g41: Circle CenterX=-14 CenterY=-18 CenterZ=0 NormalX=0 NormalY=0 NormalZ=1 AngleXU=0 Radius=1
    g42: BSplineCurve PolesCount=3 KnotsCount=2 Degree=2 IsPeriodic=0
    g43: GeomPoint X=-12.8401 Y=-17.6958 Z=0
    g44: GeomPoint X=-14 Y=-18 Z=0
    g45: LineSegment StartX=-6.2 StartY=0 StartZ=0 EndX=-7.2 EndY=0 EndZ=0
    g46: LineSegment StartX=-7.2 StartY=0 StartZ=0 EndX=-7.2 EndY=-2 EndZ=0
    g47: LineSegment StartX=-7.2 StartY=-2 StartZ=0 EndX=-6.2215 EndY=-2 EndZ=0
    g48: LineSegment StartX=-6.32538 StartY=-4 StartZ=0 EndX=-7.65538 EndY=-4 EndZ=0
    g49: LineSegment StartX=-7.65538 StartY=-4 StartZ=0 EndX=-7.65538 EndY=-5.99526 EndZ=0
    g50: LineSegment StartX=-7.65538 StartY=-5.99526 StartZ=0 EndX=-6.48644 EndY=-5.99526 EndZ=0
    g51: LineSegment StartX=-6.77343 StartY=-8 StartZ=0 EndX=-8.43343 EndY=-8 EndZ=0
    g52: LineSegment StartX=-8.43343 StartY=-8 StartZ=0 EndX=-8.43343 EndY=-10 EndZ=0
    g53: LineSegment StartX=-8.43343 StartY=-10 StartZ=0 EndX=-7.19003 EndY=-10 EndZ=0
  constraints (112):
    c: Horizontal(g0)
    c: Distance(g0) = 2
    c: Block(g0)
    c: Vertical(g1)
    c: Coincident(g2,g0)
    c: Vertical(g2)
    c: Block(g2)
    c: Coincident(g6,g2)
    c: Weight(g3) = 1
    c: Equal(g3,g4)
    c: Equal(g3,g5)
    c: InternalAlignment(g3,g6)
    c: InternalAlignment(g4,g6)
    c: InternalAlignment(g5,g6)
    c: InternalAlignment(g7,g6)
    c: InternalAlignment(g8,g6)
    c: Block(g6)
    c: Coincident(g9,g1)
    c: Coincident(g9,g6)
    c: Horizontal(g9)
    c: Vertical(g10)
    c: Block(g10)
    c: Horizontal(g11)
    c: Block(g11)
    c: Coincident(g12,g10)
    c: Horizontal(g12)
    c: Block(g12)
    c: Coincident(g13,g11)
    c: Vertical(g13)
    c: Block(g13)
    c: Coincident(g14,g10)
    c: Horizontal(g14)
    c: Block(g14)
    c: Block(g9)
    c: Block(g1)
    c: Weight(g15) = 1
    c: Equal(g15,g16)
    c: Equal(g15,g17)
    c: InternalAlignment(g15,g18)
    c: InternalAlignment(g16,g18)
    c: InternalAlignment(g17,g18)
    c: InternalAlignment(g19,g18)
    c: InternalAlignment(g20,g18)
    c: Weight(g21) = 1
    c: Equal(g21,g22)
    c: Equal(g21,g23)
    c: InternalAlignment(g21,g24)
    c: InternalAlignment(g22,g24)
    c: InternalAlignment(g23,g24)
    c: InternalAlignment(g25,g24)
    c: InternalAlignment(g26,g24)
    c: Weight(g27) = 1
    c: Equal(g27,g28)
    c: Equal(g27,g29)
    c: Coincident(g30,g14)
    c: InternalAlignment(g27,g30)
    c: InternalAlignment(g28,g30)
    c: InternalAlignment(g29,g30)
    c: InternalAlignment(g31,g30)
    c: InternalAlignment(g32,g30)
    c: Coincident(g36,g12)
    c: Weight(g33) = 1
    c: Equal(g33,g34)
    c: Equal(g33,g35)
    c: Coincident(g36,g11)
    c: InternalAlignment(g33,g36)
    c: InternalAlignment(g34,g36)
    c: InternalAlignment(g35,g36)
    c: InternalAlignment(g37,g36)
    c: InternalAlignment(g38,g36)
    c: Coincident(g42,g13)
    c: Weight(g39) = 1
    c: Equal(g39,g40)
    c: Equal(g39,g41)
    c: Coincident(g42,g1)
    c: InternalAlignment(g39,g42)
    c: InternalAlignment(g40,g42)
    c: InternalAlignment(g41,g42)
    c: InternalAlignment(g43,g42)
    c: InternalAlignment(g44,g42)
    c: Block(g18)
    c: Block(g24)
    c: Block(g30)
    c: Block(g36)
    c: Block(g42)
    c: Horizontal(g45)
    c: Coincident(g45,g0)
    c: Vertical(g46)
    c: Coincident(g46,g45)
    c: Coincident(g47,g46)
    c: Coincident(g47,g18)
    c: Horizontal(g47)
    c: Block(g46)
    c: Coincident(g48,g18)
    c: Horizontal(g48)
    c: Distance(g48) = 1.33
    c: Vertical(g49)
    c: Coincident(g49,g48)
    c: Coincident(g50,g49)
    c: Coincident(g50,g24)
    c: Horizontal(g50)
    c: Tangent(g50,g22)
    c: Horizontal(g51)
    c: Coincident(g51,g24)
    c: Block(g51)
    c: Vertical(g52)
    c: Block(g52)
    c: Coincident(g52,g51)
    c: Coincident(g53,g52)
    c: Coincident(g53,g30)
    c: Horizontal(g53)
    c: Distance(g1) = 8.5
FEATURE [Part::Feature] Face024
  shape: bbox 9.8 x 26.5 x 2e-07 mm, 1 faces, 0 solids (baked)
FEATURE [Part::Revolution] Revolve024
  Angle = 360
  Axis = (0,1,0)
  Base = (0,0,0)
  FaceMakerClass = Part::FaceMakerBullseye
  Placement = pos=(0,0,0) rot=(0,0,1;1.5708rad)
  Solid = false
  Source = -> Face024
  Symmetric = false
FEATURE [Part::Feature] Face025
  shape: bbox 9.8 x 26.5 x 2e-07 mm, 1 faces, 0 solids (baked)
FEATURE [Part::Revolution] Revolve025
  Angle = 360
  Axis = (0,1,0)
  Base = (0,0,0)
  FaceMakerClass = Part::FaceMakerBullseye
  Placement = pos=(0,0,0) rot=(0,0,1;1.5708rad)
  Solid = false
  Source = -> Face025
  Symmetric = false
FEATURE [Part::MultiFuse] Fusion033
  Placement = pos=(-18,19,36) rot=(0,0,1;0rad)
  Shapes = -> [Revolve025,Revolve024]
FEATURE [Part::Cylinder] Cylinder014
  Angle = 360
  AttacherType = Attacher::AttachEngine3D
  Height = 20
  Placement = pos=(0,0,36.15) rot=(0,0,1;0rad)
  Radius = 14.3
FEATURE [Part::Cylinder] Cylinder015
  Angle = 360
  AttacherType = Attacher::AttachEngine3D
  Height = 10
  Placement = pos=(0,0,36.15) rot=(0,0,1;0rad)
  Radius = 4
FEATURE [Part::MultiFuse] Fusion034  label="removeToCreteHoleForPlugHousing004"
  Placement = pos=(-42,19,36) rot=(0,1,0;1.5708rad)
  Shapes = -> [Cylinder014,Cylinder015]
FEATURE [Part::Cut] Cut008  label="top004"
  Base = -> Cut004
  Placement = pos=(-1,0,0) rot=(0,0,1;0rad)
  Tool = -> Fusion034
FEATURE [Part::Box] Box005  label="Cube005"
  AttacherType = Attacher::AttachEngine3D
  Height = 28
  Length = 3
  Placement = pos=(110.7,19,22) rot=(0,0,1;0rad)
  Width = 15.7
FEATURE [Part::Cylinder] Cylinder016
  Angle = 360
  AttacherType = Attacher::AttachEngine3D
  Height = 10
  Placement = pos=(0,0,36.15) rot=(0,0,1;0rad)
  Radius = 4
FEATURE [Part::Cylinder] Cylinder017
  Angle = 360
  AttacherType = Attacher::AttachEngine3D
  Height = 20
  Placement = pos=(0,0,36.15) rot=(0,0,1;0rad)
  Radius = 10.3
FEATURE [Part::MultiFuse] Fusion035  label="removeToCreteHoleForPlugHousing005"
  Placement = pos=(70,19,36) rot=(0,1,0;1.5708rad)
  Shapes = -> [Cylinder017,Cylinder016]
FEATURE [Part::Cut] Cut009  label="plugHousingTab001"
  Base = -> Box005
  Placement = pos=(-107.4,-14,0) rot=(0,0,1;0rad)
  Tool = -> Fusion035
FEATURE [Part::Box] Box006  label="Cube006"
  AttacherType = Attacher::AttachEngine3D
  Height = 28
  Length = 3
  Placement = pos=(110.7,19,22) rot=(0,0,1;0rad)
  Width = 15.7
FEATURE [Part::Cylinder] Cylinder018
  Angle = 360
  AttacherType = Attacher::AttachEngine3D
  Height = 10
  Placement = pos=(0,0,36.15) rot=(0,0,1;0rad)
  Radius = 4
FEATURE [Part::Cylinder] Cylinder019
  Angle = 360
  AttacherType = Attacher::AttachEngine3D
  Height = 20
  Placement = pos=(0,0,36.15) rot=(0,0,1;0rad)
  Radius = 10.3
FEATURE [Part::MultiFuse] Fusion036  label="removeToCreteHoleForPlugHousing006"
  Placement = pos=(70,19,36) rot=(0,1,0;1.5708rad)
  Shapes = -> [Cylinder019,Cylinder018]
FEATURE [Part::Cut] Cut010  label="plugHousingTab002"
  Base = -> Box006
  Placement = pos=(-107.4,-14,0) rot=(0,0,1;0rad)
  Tool = -> Fusion036
FEATURE [Part::MultiFuse] Fusion037
  Placement = pos=(9.6,23,0) rot=(0,0,1;3.14159rad)
  Shapes = -> [Cut009,Cut010]
FEATURE [Part::Box] Box  label="Cube"
  AttacherType = Attacher::AttachEngine3D
  Height = 10
  Length = 3
  Placement = pos=(3.3,4,12) rot=(0,0,1;0rad)
  Width = 10
FEATURE [Part::Fillet] Fillet004
  Base = -> Fusion028
  Edges = 1 edges r=2: [Edge25]
FEATURE [Part::Fillet] Fillet005  label="plugHousing046"
  Base = -> Fillet004
  Edges = 1 edges r=2: [Edge8]
FEATURE [Part::Fillet] Fillet006
  Base = -> Box
  Edges = 1 edges r=2: [Edge11]
FEATURE [Part::Box] Box007  label="Cube007"
  AttacherType = Attacher::AttachEngine3D
  Height = 10
  Length = 3
  Placement = pos=(3.3,4,50) rot=(0,0,1;0rad)
  Width = 10
FEATURE [Part::Fillet] Fillet007
  Base = -> Box007
  Edges = 1 edges r=2: [Edge12]
FEATURE [Part::Box] Box008  label="Cube008"
  AttacherType = Attacher::AttachEngine3D
  Height = 28
  Length = 4
  Placement = pos=(5,0,22) rot=(0,0,1;0rad)
  Width = 10
FEATURE [Part::Fillet] Fillet008
  Base = -> Box008
  Edges = 1 edges r=1: [Edge7]
FEATURE [Part::Fillet] Fillet009
  Base = -> Fillet008
  Edges = 1 edges r=2: [Edge5]
FEATURE [Part::Fillet] Fillet010
  Base = -> Fillet009
  Edges = 1 edges r=2: [Edge2]
FEATURE [Sketcher::SketchObject] Sketch009  label="topSketch003"
  FullyConstrained = true
  sketch-geometry (4):
    g0: LineSegment StartX=16.8446 StartY=31.512 StartZ=0 EndX=16.3251 EndY=34.4666 EndZ=0
    g1: ArcOfCircle CenterX=19 CenterY=19.2524 CenterZ=0 NormalX=0 NormalY=0 NormalZ=1 AngleXU=0 Radius=15.4476 StartAngle=1.74483 EndAngle=2.72717
    g2: ArcOfCircle CenterX=19 CenterY=19.2524 CenterZ=0 NormalX=0 NormalY=0 NormalZ=1 AngleXU=0 Radius=12.4476 StartAngle=1.74483 EndAngle=2.73189
    g3: LineSegment StartX=4.86004 StartY=25.4725 StartZ=0 EndX=7.58253 EndY=24.2107 EndZ=0
  constraints (7):
    c: Block(g0)
    c: Coincident(g1,g0)
    c: Coincident(g2,g0)
    c: Coincident(g3,g1)
    c: Coincident(g3,g2)
    c: Block(g1)
    c: Block(g2)
FEATURE [Part::Extrusion] Extrude008
  Base = -> Sketch009
  Dir = (0,0,1)
  DirMode = 2
  FaceMakerClass = Part::FaceMakerBullseye
  LengthFwd = 10
  LengthRev = 0
  Placement = pos=(0,0,31) rot=(0,0,1;0rad)
  Solid = true
  Symmetric = false
FEATURE [Part::Cylinder] Cylinder020
  Angle = 360
  AttacherType = Attacher::AttachEngine3D
  Height = 20
  Placement = pos=(0,0,36.15) rot=(0,0,1;0rad)
  Radius = 8.2
FEATURE [Part::Cylinder] Cylinder021
  Angle = 360
  AttacherType = Attacher::AttachEngine3D
  Height = 10
  Placement = pos=(0,0,36.15) rot=(0,0,1;0rad)
  Radius = 4
FEATURE [Part::MultiFuse] Fusion038  label="removeToCreteHoleForPlugHousing007"
  Placement = pos=(-42,19,36) rot=(0,1,0;1.5708rad)
  Shapes = -> [Cylinder020,Cylinder021]
FEATURE [Part::Cut] Cut011
  Base = -> Extrude008
  Tool = -> Fusion038
FEATURE [Part::Fillet] Fillet011
  Base = -> Cut011
  Edges = 1 edges r=2: [Edge1]
FEATURE [Part::Fillet] Fillet012
  Base = -> Fillet011
  Edges = 1 edges r=2.5: [Edge1]
FEATURE [Part::Fillet] Fillet013
  Base = -> Fillet012
  Edges = 1 edges r=2.5: [Edge2]
FEATURE [Part::Box] Box010  label="Cube010"
  AttacherType = Attacher::AttachEngine3D
  Height = 16
  Length = 8
  Placement = pos=(12.7,31.52,28) rot=(0,0,1;0rad)
  Width = 4
FEATURE [Sketcher::SketchObject] Sketch010  label="topSketch004"
  FullyConstrained = true
  sketch-geometry (4):
    g0: LineSegment StartX=16.8446 StartY=31.512 StartZ=0 EndX=16.3251 EndY=34.4666 EndZ=0
    g1: ArcOfCircle CenterX=19 CenterY=19.2524 CenterZ=0 NormalX=0 NormalY=0 NormalZ=1 AngleXU=0 Radius=15.4476 StartAngle=1.74483 EndAngle=2.72717
    g2: ArcOfCircle CenterX=19 CenterY=19.2524 CenterZ=0 NormalX=0 NormalY=0 NormalZ=1 AngleXU=0 Radius=12.4476 StartAngle=1.74483 EndAngle=2.73189
    g3: LineSegment StartX=4.86004 StartY=25.4725 StartZ=0 EndX=7.58253 EndY=24.2107 EndZ=0
  constraints (7):
    c: Block(g0)
    c: Coincident(g1,g0)
    c: Coincident(g2,g0)
    c: Coincident(g3,g1)
    c: Coincident(g3,g2)
    c: Block(g1)
    c: Block(g2)
FEATURE [Part::Cylinder] Cylinder022
  Angle = 360
  AttacherType = Attacher::AttachEngine3D
  Height = 10
  Placement = pos=(0,0,36.15) rot=(0,0,1;0rad)
  Radius = 4
FEATURE [Sketcher::SketchObject] Sketch011  label="topSketch005"
  FullyConstrained = true
  sketch-geometry (4):
    g0: LineSegment StartX=16.8446 StartY=31.512 StartZ=0 EndX=16.3251 EndY=34.4666 EndZ=0
    g1: ArcOfCircle CenterX=19 CenterY=19.2524 CenterZ=0 NormalX=0 NormalY=0 NormalZ=1 AngleXU=0 Radius=15.4476 StartAngle=1.74483 EndAngle=2.72717
    g2: ArcOfCircle CenterX=19 CenterY=19.2524 CenterZ=0 NormalX=0 NormalY=0 NormalZ=1 AngleXU=0 Radius=12.4476 StartAngle=1.74483 EndAngle=2.73189
    g3: LineSegment StartX=4.86004 StartY=25.4725 StartZ=0 EndX=7.58253 EndY=24.2107 EndZ=0
  constraints (7):
    c: Block(g0)
    c: Coincident(g1,g0)
    c: Coincident(g2,g0)
    c: Coincident(g3,g1)
    c: Coincident(g3,g2)
    c: Block(g1)
    c: Block(g2)
FEATURE [Part::Extrusion] Extrude010
  Base = -> Sketch011
  Dir = (0,0,1)
  DirMode = 2
  FaceMakerClass = Part::FaceMakerBullseye
  LengthFwd = 10.6
  LengthRev = 0
  Placement = pos=(0,0,31) rot=(0,0,1;0rad)
  Solid = true
  Symmetric = false
FEATURE [Part::Cylinder] Cylinder023
  Angle = 360
  AttacherType = Attacher::AttachEngine3D
  Height = 20
  Placement = pos=(0,0,36.15) rot=(0,0,1;0rad)
  Radius = 8.2
FEATURE [Part::MultiFuse] Fusion039  label="removeToCreteHoleForPlugHousing008"
  Placement = pos=(-42,19,36) rot=(0,1,0;1.5708rad)
  Shapes = -> [Cylinder023,Cylinder022]
FEATURE [Part::Cut] Cut012
  Base = -> Extrude010
  Placement = pos=(0,0,-0.3) rot=(0,0,1;0rad)
  Tool = -> Fusion039
FEATURE [Part::Cut] Cut013
  Base = -> Box010
  Tool = -> Cut012
FEATURE [Part::Fillet] Fillet014
  Base = -> Cut013
  Edges = 1 edges r=0.7: [Edge13]
FEATURE [Part::Fillet] Fillet015
  Base = -> Fillet014
  Edges = 1 edges r=0.7: [Edge13]
FEATURE [Part::Fillet] Fillet016
  Base = -> Fillet015
  Edges = 1 edges r=0.7: [Edge16]
FEATURE [Part::Fillet] Fillet017
  Base = -> Fillet016
  Edges = 1 edges r=0.7: [Edge11]
FEATURE [Part::Fillet] Fillet018
  Base = -> Fillet017
  Edges = 1 edges r=0.7: [Edge10]
FEATURE [Part::Fillet] Fillet019
  Base = -> Fillet018
  Edges = 1 edges r=1.2: [Edge5]
FEATURE [Part::Fillet] Fillet020
  Base = -> Fillet019
  Edges = 1 edges r=1.2: [Edge12]
FEATURE [Part::Fillet] Fillet021
  Base = -> Fillet020
  Edges = 1 edges r=2: [Edge1]
  Placement = pos=(0.3,0,0) rot=(0,0,1;0rad)
FEATURE [Part::MultiFuse] Fusion040  label="top005"
  Shapes = -> [Cut008,Fillet021]
FEATURE [Part::MultiFuse] Fusion041  label="wireHolder"
  Shapes = -> [Fusion033,Fillet013]
FEATURE [Part::MultiFuse] Fusion042
  Shapes = -> [Fillet007,Fusion041]
FEATURE [Part::MultiFuse] Fusion043  label="wireHolder001"
  Shapes = -> [Fusion042,Fillet010]
FEATURE [Part::MultiFuse] Fusion044  label="wireHolder002"
  Shapes = -> [Fillet006,Fusion037,Fusion043]
FEATURE [Part::Feature] Face026
  shape: bbox 11 x 6 x 2e-07 mm, 1 faces, 0 solids (baked)
FEATURE [Part::Revolution] Revolve026
  Angle = 360
  Axis = (0,1,0)
  Base = (0,0,0)
  FaceMakerClass = Part::FaceMakerBullseye
  Placement = pos=(30.3,-1,19.7) rot=(0,0,1;0rad)
  Solid = false
  Source = -> Face026
  Symmetric = false
FEATURE [Sketcher::SketchObject] Sketch013  label="topSketch006"
  FullyConstrained = true
  sketch-geometry (13):
    g0: LineSegment StartX=117 StartY=19 StartZ=0 EndX=117 EndY=38 EndZ=0
    g1: ArcOfCircle CenterX=98 CenterY=19 CenterZ=0 NormalX=0 NormalY=0 NormalZ=1 AngleXU=0 Radius=19 StartAngle=5.7297 EndAngle=6.28319
    g2: LineSegment StartX=0 StartY=3 StartZ=0 EndX=0 EndY=19 EndZ=0
    g3: LineSegment StartX=19 StartY=38 StartZ=0 EndX=117 EndY=38 EndZ=0
    g4: ArcOfCircle CenterX=19 CenterY=19 CenterZ=0 NormalX=0 NormalY=0 NormalZ=1 AngleXU=0 Radius=19 StartAngle=1.5708 EndAngle=3.14159
    g5: ArcOfCircle CenterX=19 CenterY=19 CenterZ=0 NormalX=0 NormalY=0 NormalZ=1 AngleXU=0 Radius=16 StartAngle=1.5708 EndAngle=3.14159
    g6: ArcOfCircle CenterX=98 CenterY=19 CenterZ=0 NormalX=0 NormalY=0 NormalZ=1 AngleXU=0 Radius=16 StartAngle=5.60905 EndAngle=6.28319
    g7: LineSegment StartX=114 StartY=19 StartZ=0 EndX=114 EndY=35 EndZ=0
    g8: LineSegment StartX=110.5 StartY=9.01251 StartZ=0 EndX=114.163 EndY=9.01251 EndZ=0
    g9: LineSegment StartX=114 StartY=35 StartZ=0 EndX=19 EndY=35 EndZ=0
    g10: LineSegment StartX=0 StartY=3 StartZ=0 EndX=0 EndY=0 EndZ=0
    g11: LineSegment StartX=3 StartY=0 StartZ=0 EndX=0 EndY=0 EndZ=0
    g12: LineSegment StartX=3 StartY=19 StartZ=0 EndX=3 EndY=0 EndZ=0
  constraints (33):
    c: Vertical(g0)
    c: Distance(g0) = 19
    c: Block(g0)
    c: Coincident(g1,g0)
    c: Block(g1)
    c: Vertical(g2)
    c: Block(g2)
    c: Coincident(g3,g0)
    c: Horizontal(g3)
    c: Distance(g3) = 98
    c: Coincident(g4,g3)
    c: Coincident(g4,g2)
    c: Block(g4)
    c: Coincident(g5,g4)
    c: Coincident(g6,g1)
    c: Block(g6)
    c: Block(g5)
    c: Coincident(g7,g6)
    c: Vertical(g7)
    c: Coincident(g8,g6)
    c: Coincident(g8,g1)
    c: Coincident(g9,g7)
    c: Coincident(g9,g5)
    c: Horizontal(g9)
    c: Tangent(g9,g5)
    c: Coincident(g10,g2)
    c: Distance(g10) = 3
    c: Vertical(g10)
    c: Coincident(g11,g10)
    c: Horizontal(g11)
    c: Coincident(g12,g5)
    c: Coincident(g12,g11)
    c: Vertical(g12)
FEATURE [Part::Extrusion] Extrude011  label="top006"
  Base = -> Sketch013
  Dir = (0,0,1)
  DirMode = 2
  FaceMakerClass = Part::FaceMakerBullseye
  LengthFwd = 72
  LengthRev = 0
  Solid = true
  Symmetric = false
FEATURE [Sketcher::SketchObject] Sketch014
  FullyConstrained = true
  MapMode = 3
  Placement = pos=(0,0,0) rot=(1,0,0;1.5708rad)
  Support = -> [Extrude011]
  sketch-geometry (8):
    g0: Circle CenterX=80.351 CenterY=-67.6202 CenterZ=0 NormalX=0 NormalY=0 NormalZ=1 AngleXU=0 Radius=2
    g1: Circle CenterX=80.351 CenterY=-67.6202 CenterZ=0 NormalX=0 NormalY=0 NormalZ=1 AngleXU=0 Radius=3
    g2: Circle CenterX=80.351 CenterY=-4.92017 CenterZ=0 NormalX=0 NormalY=0 NormalZ=1 AngleXU=0 Radius=2
    g3: Circle CenterX=80.351 CenterY=-4.92017 CenterZ=0 NormalX=0 NormalY=0 NormalZ=1 AngleXU=0 Radius=3
    g4: Circle CenterX=23.851 CenterY=-4.92017 CenterZ=0 NormalX=0 NormalY=0 NormalZ=1 AngleXU=0 Radius=2
    g5: Circle CenterX=23.851 CenterY=-4.92017 CenterZ=0 NormalX=0 NormalY=0 NormalZ=1 AngleXU=0 Radius=3
    g6: Circle CenterX=23.851 CenterY=-67.6202 CenterZ=0 NormalX=0 NormalY=0 NormalZ=1 AngleXU=0 Radius=2
    g7: Circle CenterX=23.851 CenterY=-67.6202 CenterZ=0 NormalX=0 NormalY=0 NormalZ=1 AngleXU=0 Radius=3
  constraints (8):
    c: Block(g3)
    c: Block(g2)
    c: Block(g1)
    c: Block(g0)
    c: Block(g6)
    c: Block(g7)
    c: Block(g4)
    c: Block(g5)
FEATURE [Part::Feature] Face027
  shape: bbox 11 x 6 x 2e-07 mm, 1 faces, 0 solids (baked)
FEATURE [Part::Revolution] Revolve027
  Angle = 360
  Axis = (0,1,0)
  Base = (0,0,0)
  FaceMakerClass = Part::FaceMakerBullseye
  Placement = pos=(30.3,-1,51.7) rot=(0,0,1;0rad)
  Solid = false
  Source = -> Face027
  Symmetric = false
FEATURE [Part::Feature] Face028
  shape: bbox 11 x 6 x 2e-07 mm, 1 faces, 0 solids (baked)
FEATURE [Part::Revolution] Revolve028
  Angle = 360
  Axis = (0,1,0)
  Base = (0,0,0)
  FaceMakerClass = Part::FaceMakerBullseye
  Placement = pos=(62.3,-1,19.7) rot=(0,0,1;0rad)
  Solid = false
  Source = -> Face028
  Symmetric = false
FEATURE [Part::Feature] Face029
  shape: bbox 11 x 6 x 2e-07 mm, 1 faces, 0 solids (baked)
FEATURE [Part::Revolution] Revolve029
  Angle = 360
  Axis = (0,1,0)
  Base = (0,0,0)
  FaceMakerClass = Part::FaceMakerBullseye
  Placement = pos=(62.3,-1,51.7) rot=(0,0,1;0rad)
  Solid = false
  Source = -> Face029
  Symmetric = false
FEATURE [Part::Feature] Wire
  shape: bbox 11 x 5.2 x 2e-07 mm, 0 faces, 0 solids (baked)
FEATURE [Part::Revolution] Revolve030
  Angle = 360
  Axis = (0,1,0)
  Base = (0,0,0)
  FaceMakerClass = Part::FaceMakerBullseye
  Placement = pos=(30.3,38,19.7) rot=(0,0,1;0rad)
  Solid = true
  Source = -> Wire
  Symmetric = false
FEATURE [Part::Feature] Wire001
  shape: bbox 11 x 5.2 x 2e-07 mm, 0 faces, 0 solids (baked)
FEATURE [Part::Revolution] Revolve031
  Angle = 360
  Axis = (0,1,0)
  Base = (0,0,0)
  FaceMakerClass = Part::FaceMakerBullseye
  Placement = pos=(30.3,38,51.7) rot=(0,0,1;0rad)
  Solid = true
  Source = -> Wire001
  Symmetric = false
FEATURE [Part::Feature] Wire002
  shape: bbox 11 x 5.2 x 2e-07 mm, 0 faces, 0 solids (baked)
FEATURE [Part::Revolution] Revolve032
  Angle = 360
  Axis = (0,1,0)
  Base = (0,0,0)
  FaceMakerClass = Part::FaceMakerBullseye
  Placement = pos=(62.3,38,51.7) rot=(0,0,1;0rad)
  Solid = true
  Source = -> Wire002
  Symmetric = false
FEATURE [Part::Feature] Wire003
  shape: bbox 11 x 5.2 x 2e-07 mm, 0 faces, 0 solids (baked)
FEATURE [Part::Revolution] Revolve033
  Angle = 360
  Axis = (0,1,0)
  Base = (0,0,0)
  FaceMakerClass = Part::FaceMakerBullseye
  Placement = pos=(62.3,38,19.7) rot=(0,0,1;0rad)
  Solid = true
  Source = -> Wire003
  Symmetric = false
FEATURE [Part::MultiFuse] Fusion045  label="altRandScrewHousing"
  Shapes = -> [Revolve029,Revolve027,Revolve028,Revolve026]
FEATURE [Part::MultiFuse] Fusion046  label="fanScrewHousing"
  Shapes = -> [Revolve033,Revolve032,Revolve031,Revolve030]
FEATURE [Sketcher::SketchObject] Sketch015
  FullyConstrained = true
  sketch-geometry (17):
    g0: Circle CenterX=-3.5 CenterY=23.5 CenterZ=0 NormalX=0 NormalY=0 NormalZ=1 AngleXU=0 Radius=1
    g1: Circle CenterX=-1 CenterY=15.25 CenterZ=0 NormalX=0 NormalY=0 NormalZ=1 AngleXU=0 Radius=1
    g2: Circle CenterX=-3.5 CenterY=7 CenterZ=0 NormalX=0 NormalY=0 NormalZ=1 AngleXU=0 Radius=1
    g3: BSplineCurve PolesCount=3 KnotsCount=2 Degree=2 IsPeriodic=0
    g4: GeomPoint X=-3.5 Y=23.5 Z=0
    g5: GeomPoint X=-3.5 Y=7 Z=0
    g6: Circle CenterX=-4.8 CenterY=30.5 CenterZ=0 NormalX=0 NormalY=0 NormalZ=1 AngleXU=0 Radius=1
    g7: Circle CenterX=-3.5 CenterY=30.5 CenterZ=0 NormalX=0 NormalY=0 NormalZ=1 AngleXU=0 Radius=1
    g8: Circle CenterX=-3.5 CenterY=29.2 CenterZ=0 NormalX=0 NormalY=0 NormalZ=1 AngleXU=0 Radius=1
    g9: BSplineCurve PolesCount=3 KnotsCount=2 Degree=2 IsPeriodic=0
    g10: GeomPoint X=-4.8 Y=30.5 Z=0
    g11: GeomPoint X=-3.5 Y=29.2 Z=0
    g12: LineSegment StartX=-3.5 StartY=29.2 StartZ=0 EndX=-3.5 EndY=23.5 EndZ=0
    g13: LineSegment StartX=-4.8 StartY=30.5 StartZ=0 EndX=0 EndY=30.5 EndZ=0
    g14: LineSegment StartX=-3.5 StartY=0.3 StartZ=0 EndX=0 EndY=0.3 EndZ=0
    g15: LineSegment StartX=-3.5 StartY=0.3 StartZ=0 EndX=-3.5 EndY=7 EndZ=0
    g16: LineSegment StartX=0 StartY=0.3 StartZ=0 EndX=0 EndY=30.5 EndZ=0
  constraints (33):
    c: Weight(g0) = 1
    c: Equal(g0,g1)
    c: Equal(g0,g2)
    c: InternalAlignment(g0,g3)
    c: InternalAlignment(g1,g3)
    c: InternalAlignment(g2,g3)
    c: InternalAlignment(g4,g3)
    c: InternalAlignment(g5,g3)
    c: Block(g3)
    c: Weight(g6) = 1
    c: Equal(g6,g7)
    c: Equal(g6,g8)
    c: InternalAlignment(g6,g9)
    c: InternalAlignment(g7,g9)
    c: InternalAlignment(g8,g9)
    c: InternalAlignment(g10,g9)
    c: InternalAlignment(g11,g9)
    c: Block(g9)
    c: Coincident(g12,g9)
    c: Coincident(g12,g3)
    c: Vertical(g12)
    c: Coincident(g13,g9)
    c: Horizontal(g13)
    c: Distance(g13) = 4.8
    c: Horizontal(g14)
    c: Block(g14)
    c: Coincident(g15,g14)
    c: Coincident(g15,g3)
    c: Vertical(g15)
    c: Coincident(g16,g14)
    c: Coincident(g16,g13)
    c: Vertical(g16)
    c: Tangent(g16,g1)
FEATURE [Sketcher::SketchObject] Sketch016
  FullyConstrained = true
  sketch-geometry (16):
    g0: Circle CenterX=-3.5 CenterY=23.5 CenterZ=0 NormalX=0 NormalY=0 NormalZ=1 AngleXU=0 Radius=1
    g1: Circle CenterX=-1 CenterY=15.25 CenterZ=0 NormalX=0 NormalY=0 NormalZ=1 AngleXU=0 Radius=1
    g2: Circle CenterX=-3.5 CenterY=7 CenterZ=0 NormalX=0 NormalY=0 NormalZ=1 AngleXU=0 Radius=1
    g3: BSplineCurve PolesCount=3 KnotsCount=2 Degree=2 IsPeriodic=0
    g4: GeomPoint X=-3.5 Y=23.5 Z=0
    g5: GeomPoint X=-3.5 Y=7 Z=0
    g6: LineSegment StartX=-3.5 StartY=28.2 StartZ=0 EndX=-3.5 EndY=23.5 EndZ=0
    g7: LineSegment StartX=0 StartY=29.5 StartZ=0 EndX=0 EndY=30 EndZ=0
    g8: LineSegment StartX=-3.5 StartY=28.2 StartZ=0 EndX=-3.5 EndY=30 EndZ=0
    g9: LineSegment StartX=0 StartY=30 StartZ=0 EndX=0 EndY=30.5 EndZ=0
    g10: LineSegment StartX=0 StartY=30.5 StartZ=0 EndX=-3.5 EndY=30.5 EndZ=0
    g11: LineSegment StartX=-3.5 StartY=30.5 StartZ=0 EndX=-3.5 EndY=30 EndZ=0
    g12: LineSegment StartX=0 StartY=29.5 StartZ=0 EndX=0 EndY=5 EndZ=0
    g13: LineSegment StartX=-3.5 StartY=0.3 StartZ=0 EndX=-3.5 EndY=7 EndZ=0
    g14: LineSegment StartX=-3.5 StartY=0.3 StartZ=0 EndX=0 EndY=0.3 EndZ=0
    g15: LineSegment StartX=0 StartY=5 StartZ=0 EndX=0 EndY=0.3 EndZ=0
  constraints (39):
    c: Weight(g0) = 1
    c: Equal(g0,g1)
    c: Equal(g0,g2)
    c: InternalAlignment(g0,g3)
    c: InternalAlignment(g1,g3)
    c: InternalAlignment(g2,g3)
    c: InternalAlignment(g4,g3)
    c: InternalAlignment(g5,g3)
    c: Block(g3)
    c: Coincident(g6,g3)
    c: Vertical(g6)
    c: Vertical(g7)
    c: Distance(g7) = 0.5
    c: Coincident(g8,g6)
    c: Vertical(g8)
    c: Block(g6)
    c: Block(g7)
    c: Vertical(g9)
    c: Equal(g7,g9) = 0.5
    c: Block(g9)
    c: Coincident(g9,g7)
    c: Horizontal(g10)
    c: Coincident(g10,g9)
    c: Coincident(g11,g10)
    c: Coincident(g11,g8)
    c: Vertical(g11)
    c: Block(g11)
    c: Coincident(g12,g7)
    c: Vertical(g12)
    c: Coincident(g13,g3)
    c: Vertical(g13)
    c: Distance(g13) = 6.7
    c: Coincident(g14,g13)
    c: Horizontal(g14)
    c: Block(g14)
    c: Coincident(g15,g12)
    c: Coincident(g15,g14)
    c: Vertical(g15)
    c: Block(g15)
FEATURE [Sketcher::SketchObject] Sketch017
  FullyConstrained = true
  sketch-geometry (11):
    g0: LineSegment StartX=-3.5 StartY=1e-16 StartZ=0 EndX=-1.6 EndY=1e-16 EndZ=0
    g1: LineSegment StartX=-1.6 StartY=1e-16 StartZ=0 EndX=-1.6 EndY=1.5 EndZ=0
    g2: LineSegment StartX=-3.5 StartY=1.5 StartZ=0 EndX=-1.6 EndY=1.5 EndZ=0
    g3: LineSegment StartX=-3.5 StartY=1e-16 StartZ=0 EndX=-4.8 EndY=1e-16 EndZ=0
    g4: Circle CenterX=-3.5 CenterY=1.3 CenterZ=0 NormalX=0 NormalY=0 NormalZ=1 AngleXU=0 Radius=1
    g5: Circle CenterX=-3.5 CenterY=1e-16 CenterZ=0 NormalX=0 NormalY=0 NormalZ=1 AngleXU=0 Radius=1
    g6: Circle CenterX=-4.8 CenterY=1e-16 CenterZ=0 NormalX=0 NormalY=0 NormalZ=1 AngleXU=0 Radius=1
    g7: BSplineCurve PolesCount=3 KnotsCount=2 Degree=2 IsPeriodic=0
    g8: GeomPoint X=-3.5 Y=1.3 Z=0
    g9: GeomPoint X=-4.8 Y=1e-16 Z=0
    g10: LineSegment StartX=-3.5 StartY=1.3 StartZ=0 EndX=-3.5 EndY=1.5 EndZ=0
  constraints (24):
    c: Horizontal(g0)
    c: Distance(g0) = 1.9
    c: Block(g0)
    c: Coincident(g1,g0)
    c: Vertical(g1)
    c: Coincident(g2,g1)
    c: Horizontal(g2)
    c: Coincident(g3,g0)
    c: Horizontal(g3)
    c: Distance(g3) = 1.3
    c: Weight(g4) = 1
    c: Equal(g4,g5)
    c: Coincident(g5,g0)
    c: Equal(g4,g6)
    c: Coincident(g7,g3)
    c: InternalAlignment(g4,g7)
    c: InternalAlignment(g5,g7)
    c: InternalAlignment(g6,g7)
    c: InternalAlignment(g8,g7)
    c: InternalAlignment(g9,g7)
    c: Coincident(g10,g7)
    c: Coincident(g10,g2)
    c: Vertical(g10)
    c: Block(g10)
FEATURE [Part::Feature] Face035
  shape: bbox 3.2 x 1.5 x 2e-07 mm, 1 faces, 0 solids (baked)
FEATURE [Part::Revolution] Revolve039  label="backCaseScrewRetainer"
  Angle = 360
  Axis = (0,1,0)
  Base = (0,0,0)
  FaceMakerClass = Part::FaceMakerBullseye
  Placement = pos=(12.5,3,62) rot=(0,0,1;0rad)
  Solid = false
  Source = -> Face035
  Symmetric = false
FEATURE [Part::Feature] Face036
  shape: bbox 3.2 x 1.5 x 2e-07 mm, 1 faces, 0 solids (baked)
FEATURE [Part::Feature] Face039
  shape: bbox 4.8 x 30.2 x 2e-07 mm, 1 faces, 0 solids (baked)
FEATURE [Part::Revolution] Revolve043  label="frontCaseScrewPost002"
  Angle = 360
  Axis = (0,1,0)
  Base = (0,0,0)
  FaceMakerClass = Part::FaceMakerBullseye
  Placement = pos=(89.5,4.5,3.5) rot=(0,0,1;0rad)
  Solid = false
  Source = -> Face039
  Symmetric = false
FEATURE [Part::Feature] Face042
  shape: bbox 4.8 x 30.2 x 2e-07 mm, 1 faces, 0 solids (baked)
FEATURE [Part::Revolution] Revolve046  label="frontCaseScrewPost003"
  Angle = 360
  Axis = (0,1,0)
  Base = (0,0,0)
  FaceMakerClass = Part::FaceMakerBullseye
  Placement = pos=(89.5,4.5,68.5) rot=(0,0,1;0rad)
  Solid = false
  Source = -> Face042
  Symmetric = false
FEATURE [Part::Feature] Face043
  shape: bbox 3.2 x 1.5 x 2e-07 mm, 1 faces, 0 solids (baked)
FEATURE [Part::Revolution] Revolve047  label="frontCaseScrewRetainer002"
  Angle = 360
  Axis = (0,1,0)
  Base = (0,0,0)
  FaceMakerClass = Part::FaceMakerBullseye
  Placement = pos=(89.5,3,68.5) rot=(0,0,1;0rad)
  Solid = false
  Source = -> Face043
  Symmetric = false
FEATURE [Part::Feature] Face044
  shape: bbox 3.2 x 1.5 x 2e-07 mm, 1 faces, 0 solids (baked)
FEATURE [Part::Revolution] Revolve048  label="frontCaseScrewRetainer003"
  Angle = 360
  Axis = (0,1,0)
  Base = (0,0,0)
  FaceMakerClass = Part::FaceMakerBullseye
  Placement = pos=(89.5,3,3.5) rot=(0,0,1;0rad)
  Solid = false
  Source = -> Face044
  Symmetric = false
FEATURE [App::MeasureDistance] Distance002  label="Distance: 1.67 mm"
  Distance = 1.66921
  P1 = (99.2361,4.7524,71.7)
  P2 = (99.2347,6.42161,71.7)
FEATURE [Sketcher::SketchObject] Sketch018
  FullyConstrained = true
  sketch-geometry (7):
    g0: LineSegment StartX=0 StartY=0 StartZ=0 EndX=0 EndY=6 EndZ=0
    g1: Circle CenterX=0 CenterY=0 CenterZ=0 NormalX=0 NormalY=0 NormalZ=1 AngleXU=0 Radius=1
    g2: Circle CenterX=8 CenterY=6 CenterZ=0 NormalX=0 NormalY=0 NormalZ=1 AngleXU=0 Radius=1
    g3: BSplineCurve PolesCount=3 KnotsCount=2 Degree=2 IsPeriodic=0
    g4: GeomPoint X=0 Y=0 Z=0
    g5: GeomPoint X=8 Y=6 Z=0
    g6: LineSegment StartX=0 StartY=6 StartZ=0 EndX=8 EndY=6 EndZ=0
  constraints (14):
    c: Coincident(g0,g-1)
    c: Distance(g0) = 6
    c: Vertical(g0)
    c: Coincident(g3,g0)
    c: Weight(g1) = 1
    c: Equal(g1,g2)
    c: InternalAlignment(g1,g3)
    c: InternalAlignment(g2,g3)
    c: InternalAlignment(g4,g3)
    c: InternalAlignment(g5,g3)
    c: Block(g3)
    c: Coincident(g6,g0)
    c: Coincident(g6,g3)
    c: Horizontal(g6)
FEATURE [Part::Extrusion] Extrude012  label="caseScrewPillarBracket"
  Base = -> Sketch018
  Dir = (0,0,1)
  DirMode = 2
  FaceMakerClass = Part::FaceMakerBullseye
  LengthFwd = 2.4
  LengthRev = 0
  Placement = pos=(15.76,29,8.8) rot=(0,1,0;0rad)
  Solid = true
  Symmetric = false
FEATURE [Sketcher::SketchObject] Sketch019
  FullyConstrained = true
  sketch-geometry (7):
    g0: LineSegment StartX=0 StartY=0 StartZ=0 EndX=0 EndY=6 EndZ=0
    g1: Circle CenterX=0 CenterY=0 CenterZ=0 NormalX=0 NormalY=0 NormalZ=1 AngleXU=0 Radius=1
    g2: Circle CenterX=8 CenterY=6 CenterZ=0 NormalX=0 NormalY=0 NormalZ=1 AngleXU=0 Radius=1
    g3: BSplineCurve PolesCount=3 KnotsCount=2 Degree=2 IsPeriodic=0
    g4: GeomPoint X=0 Y=0 Z=0
    g5: GeomPoint X=8 Y=6 Z=0
    g6: LineSegment StartX=0 StartY=6 StartZ=0 EndX=8 EndY=6 EndZ=0
  constraints (14):
    c: Coincident(g0,g-1)
    c: Distance(g0) = 6
    c: Vertical(g0)
    c: Coincident(g3,g0)
    c: Weight(g1) = 1
    c: Equal(g1,g2)
    c: InternalAlignment(g1,g3)
    c: InternalAlignment(g2,g3)
    c: InternalAlignment(g4,g3)
    c: InternalAlignment(g5,g3)
    c: Block(g3)
    c: Coincident(g6,g0)
    c: Coincident(g6,g3)
    c: Horizontal(g6)
FEATURE [Part::Extrusion] Extrude013  label="caseScrewPillarBracket001"
  Base = -> Sketch019
  Dir = (0,0,1)
  DirMode = 2
  FaceMakerClass = Part::FaceMakerBullseye
  LengthFwd = 2.4
  LengthRev = 0
  Placement = pos=(15.76,29,60.8) rot=(0,0,1;0rad)
  Solid = true
  Symmetric = false
FEATURE [Sketcher::SketchObject] Sketch020
  FullyConstrained = true
  sketch-geometry (7):
    g0: LineSegment StartX=0 StartY=0 StartZ=0 EndX=0 EndY=6 EndZ=0
    g1: Circle CenterX=0 CenterY=0 CenterZ=0 NormalX=0 NormalY=0 NormalZ=1 AngleXU=0 Radius=1
    g2: Circle CenterX=8 CenterY=6 CenterZ=0 NormalX=0 NormalY=0 NormalZ=1 AngleXU=0 Radius=1
    g3: BSplineCurve PolesCount=3 KnotsCount=2 Degree=2 IsPeriodic=0
    g4: GeomPoint X=0 Y=0 Z=0
    g5: GeomPoint X=8 Y=6 Z=0
    g6: LineSegment StartX=0 StartY=6 StartZ=0 EndX=8 EndY=6 EndZ=0
  constraints (14):
    c: Coincident(g0,g-1)
    c: Distance(g0) = 6
    c: Vertical(g0)
    c: Coincident(g3,g0)
    c: Weight(g1) = 1
    c: Equal(g1,g2)
    c: InternalAlignment(g1,g3)
    c: InternalAlignment(g2,g3)
    c: InternalAlignment(g4,g3)
    c: InternalAlignment(g5,g3)
    c: Block(g3)
    c: Coincident(g6,g0)
    c: Coincident(g6,g3)
    c: Horizontal(g6)
FEATURE [Part::Extrusion] Extrude014  label="caseScrewPillarBracket002"
  Base = -> Sketch020
  Dir = (0,0,1)
  DirMode = 2
  FaceMakerClass = Part::FaceMakerBullseye
  LengthFwd = 2.4
  LengthRev = 0
  Placement = pos=(13.7,29,13.26) rot=(0,1,0;-1.5708rad)
  Solid = true
  Symmetric = false
FEATURE [Sketcher::SketchObject] Sketch021
  FullyConstrained = true
  sketch-geometry (7):
    g0: LineSegment StartX=0 StartY=0 StartZ=0 EndX=0 EndY=6 EndZ=0
    g1: Circle CenterX=0 CenterY=0 CenterZ=0 NormalX=0 NormalY=0 NormalZ=1 AngleXU=0 Radius=1
    g2: Circle CenterX=8 CenterY=6 CenterZ=0 NormalX=0 NormalY=0 NormalZ=1 AngleXU=0 Radius=1
    g3: BSplineCurve PolesCount=3 KnotsCount=2 Degree=2 IsPeriodic=0
    g4: GeomPoint X=0 Y=0 Z=0
    g5: GeomPoint X=8 Y=6 Z=0
    g6: LineSegment StartX=0 StartY=6 StartZ=0 EndX=8 EndY=6 EndZ=0
  constraints (14):
    c: Coincident(g0,g-1)
    c: Distance(g0) = 6
    c: Vertical(g0)
    c: Coincident(g3,g0)
    c: Weight(g1) = 1
    c: Equal(g1,g2)
    c: InternalAlignment(g1,g3)
    c: InternalAlignment(g2,g3)
    c: InternalAlignment(g4,g3)
    c: InternalAlignment(g5,g3)
    c: Block(g3)
    c: Coincident(g6,g0)
    c: Coincident(g6,g3)
    c: Horizontal(g6)
FEATURE [Part::Extrusion] Extrude015  label="caseScrewPillarBracket003"
  Base = -> Sketch021
  Dir = (0,0,1)
  DirMode = 2
  FaceMakerClass = Part::FaceMakerBullseye
  LengthFwd = 2.4
  LengthRev = 0
  Placement = pos=(11.3,29,58.74) rot=(0,1,0;1.5708rad)
  Solid = true
  Symmetric = false
FEATURE [Sketcher::SketchObject] Sketch022
  FullyConstrained = true
  sketch-geometry (7):
    g0: LineSegment StartX=0 StartY=0 StartZ=0 EndX=0 EndY=6 EndZ=0
    g1: Circle CenterX=0 CenterY=0 CenterZ=0 NormalX=0 NormalY=0 NormalZ=1 AngleXU=0 Radius=1
    g2: Circle CenterX=8 CenterY=6 CenterZ=0 NormalX=0 NormalY=0 NormalZ=1 AngleXU=0 Radius=1
    g3: BSplineCurve PolesCount=3 KnotsCount=2 Degree=2 IsPeriodic=0
    g4: GeomPoint X=0 Y=0 Z=0
    g5: GeomPoint X=8 Y=6 Z=0
    g6: LineSegment StartX=0 StartY=6 StartZ=0 EndX=8 EndY=6 EndZ=0
  constraints (14):
    c: Coincident(g0,g-1)
    c: Distance(g0) = 6
    c: Vertical(g0)
    c: Coincident(g3,g0)
    c: Weight(g1) = 1
    c: Equal(g1,g2)
    c: InternalAlignment(g1,g3)
    c: InternalAlignment(g2,g3)
    c: InternalAlignment(g4,g3)
    c: InternalAlignment(g5,g3)
    c: Block(g3)
    c: Coincident(g6,g0)
    c: Coincident(g6,g3)
    c: Horizontal(g6)
FEATURE [Part::Extrusion] Extrude016  label="caseScrewPillarBracket004"
  Base = -> Sketch022
  Dir = (0,0,1)
  DirMode = 2
  FaceMakerClass = Part::FaceMakerBullseye
  LengthFwd = 2.4
  LengthRev = 0
  Placement = pos=(88.3,29,65.23) rot=(0,1,0;1.5708rad)
  Solid = true
  Symmetric = false
FEATURE [Sketcher::SketchObject] Sketch023
  FullyConstrained = true
  sketch-geometry (7):
    g0: LineSegment StartX=0 StartY=0 StartZ=0 EndX=0 EndY=6 EndZ=0
    g1: Circle CenterX=0 CenterY=0 CenterZ=0 NormalX=0 NormalY=0 NormalZ=1 AngleXU=0 Radius=1
    g2: Circle CenterX=8 CenterY=6 CenterZ=0 NormalX=0 NormalY=0 NormalZ=1 AngleXU=0 Radius=1
    g3: BSplineCurve PolesCount=3 KnotsCount=2 Degree=2 IsPeriodic=0
    g4: GeomPoint X=0 Y=0 Z=0
    g5: GeomPoint X=8 Y=6 Z=0
    g6: LineSegment StartX=0 StartY=6 StartZ=0 EndX=8 EndY=6 EndZ=0
  constraints (14):
    c: Coincident(g0,g-1)
    c: Distance(g0) = 6
    c: Vertical(g0)
    c: Coincident(g3,g0)
    c: Weight(g1) = 1
    c: Equal(g1,g2)
    c: InternalAlignment(g1,g3)
    c: InternalAlignment(g2,g3)
    c: InternalAlignment(g4,g3)
    c: InternalAlignment(g5,g3)
    c: Block(g3)
    c: Coincident(g6,g0)
    c: Coincident(g6,g3)
    c: Horizontal(g6)
FEATURE [Part::Extrusion] Extrude017  label="caseScrewPillarBracket005"
  Base = -> Sketch023
  Dir = (0,0,1)
  DirMode = 2
  FaceMakerClass = Part::FaceMakerBullseye
  LengthFwd = 2.4
  LengthRev = 0
  Placement = pos=(90.7,29,6.77) rot=(0,-1,0;1.5708rad)
  Solid = true
  Symmetric = false
FEATURE [Sketcher::SketchObject] Sketch024
  FullyConstrained = true
  sketch-geometry (7):
    g0: LineSegment StartX=0 StartY=0 StartZ=0 EndX=0 EndY=6 EndZ=0
    g1: Circle CenterX=0 CenterY=0 CenterZ=0 NormalX=0 NormalY=0 NormalZ=1 AngleXU=0 Radius=1
    g2: Circle CenterX=8 CenterY=6 CenterZ=0 NormalX=0 NormalY=0 NormalZ=1 AngleXU=0 Radius=1
    g3: BSplineCurve PolesCount=3 KnotsCount=2 Degree=2 IsPeriodic=0
    g4: GeomPoint X=0 Y=0 Z=0
    g5: GeomPoint X=8 Y=6 Z=0
    g6: LineSegment StartX=0 StartY=6 StartZ=0 EndX=8 EndY=6 EndZ=0
  constraints (14):
    c: Coincident(g0,g-1)
    c: Distance(g0) = 6
    c: Vertical(g0)
    c: Coincident(g3,g0)
    c: Weight(g1) = 1
    c: Equal(g1,g2)
    c: InternalAlignment(g1,g3)
    c: InternalAlignment(g2,g3)
    c: InternalAlignment(g4,g3)
    c: InternalAlignment(g5,g3)
    c: Block(g3)
    c: Coincident(g6,g0)
    c: Coincident(g6,g3)
    c: Horizontal(g6)
FEATURE [Part::Extrusion] Extrude018  label="caseScrewPillarBracket006"
  Base = -> Sketch024
  Dir = (0,0,1)
  DirMode = 2
  FaceMakerClass = Part::FaceMakerBullseye
  LengthFwd = 2.4
  LengthRev = 0
  Placement = pos=(103.7,29,6.77) rot=(0,-1,0;1.5708rad)
  Solid = true
  Symmetric = false
FEATURE [Sketcher::SketchObject] Sketch025
  FullyConstrained = true
  sketch-geometry (7):
    g0: LineSegment StartX=0 StartY=0 StartZ=0 EndX=0 EndY=6 EndZ=0
    g1: Circle CenterX=0 CenterY=0 CenterZ=0 NormalX=0 NormalY=0 NormalZ=1 AngleXU=0 Radius=1
    g2: Circle CenterX=8 CenterY=6 CenterZ=0 NormalX=0 NormalY=0 NormalZ=1 AngleXU=0 Radius=1
    g3: BSplineCurve PolesCount=3 KnotsCount=2 Degree=2 IsPeriodic=0
    g4: GeomPoint X=0 Y=0 Z=0
    g5: GeomPoint X=8 Y=6 Z=0
    g6: LineSegment StartX=0 StartY=6 StartZ=0 EndX=8 EndY=6 EndZ=0
  constraints (14):
    c: Coincident(g0,g-1)
    c: Distance(g0) = 6
    c: Vertical(g0)
    c: Coincident(g3,g0)
    c: Weight(g1) = 1
    c: Equal(g1,g2)
    c: InternalAlignment(g1,g3)
    c: InternalAlignment(g2,g3)
    c: InternalAlignment(g4,g3)
    c: InternalAlignment(g5,g3)
    c: Block(g3)
    c: Coincident(g6,g0)
    c: Coincident(g6,g3)
    c: Horizontal(g6)
FEATURE [Part::Extrusion] Extrude019  label="caseScrewPillarBracket007"
  Base = -> Sketch025
  Dir = (0,0,1)
  DirMode = 2
  FaceMakerClass = Part::FaceMakerBullseye
  LengthFwd = 2.4
  LengthRev = 0
  Placement = pos=(101.3,29,65.23) rot=(0,1,0;1.5708rad)
  Solid = true
  Symmetric = false
FEATURE [Part::Box] Box011  label="frontCaseScrewPillarBracket"
  AttacherType = Attacher::AttachEngine3D
  Height = 2.4
  Length = 16
  Placement = pos=(87,28,2.3) rot=(0,0,1;0rad)
  Width = 7
FEATURE [Part::Box] Box012  label="frontCaseScrewPillarBracket001"
  AttacherType = Attacher::AttachEngine3D
  Height = 2.4
  Length = 16
  Placement = pos=(87,28,67.3) rot=(0,0,1;0rad)
  Width = 7
FEATURE [Sketcher::SketchObject] Sketch026
  FullyConstrained = true
  sketch-geometry (17):
    g0: Circle CenterX=-3.5 CenterY=23.5 CenterZ=0 NormalX=0 NormalY=0 NormalZ=1 AngleXU=0 Radius=1
    g1: Circle CenterX=-1 CenterY=15.25 CenterZ=0 NormalX=0 NormalY=0 NormalZ=1 AngleXU=0 Radius=1
    g2: Circle CenterX=-3.5 CenterY=7 CenterZ=0 NormalX=0 NormalY=0 NormalZ=1 AngleXU=0 Radius=1
    g3: BSplineCurve PolesCount=3 KnotsCount=2 Degree=2 IsPeriodic=0
    g4: GeomPoint X=-3.5 Y=23.5 Z=0
    g5: GeomPoint X=-3.5 Y=7 Z=0
    g6: Circle CenterX=-4.8 CenterY=30.5 CenterZ=0 NormalX=0 NormalY=0 NormalZ=1 AngleXU=0 Radius=1
    g7: Circle CenterX=-3.5 CenterY=30.5 CenterZ=0 NormalX=0 NormalY=0 NormalZ=1 AngleXU=0 Radius=1
    g8: Circle CenterX=-3.5 CenterY=29.2 CenterZ=0 NormalX=0 NormalY=0 NormalZ=1 AngleXU=0 Radius=1
    g9: BSplineCurve PolesCount=3 KnotsCount=2 Degree=2 IsPeriodic=0
    g10: GeomPoint X=-4.8 Y=30.5 Z=0
    g11: GeomPoint X=-3.5 Y=29.2 Z=0
    g12: LineSegment StartX=-3.5 StartY=29.2 StartZ=0 EndX=-3.5 EndY=23.5 EndZ=0
    g13: LineSegment StartX=-4.8 StartY=30.5 StartZ=0 EndX=0 EndY=30.5 EndZ=0
    g14: LineSegment StartX=-3.5 StartY=5 StartZ=0 EndX=-3.5 EndY=7 EndZ=0
    g15: LineSegment StartX=0 StartY=5 StartZ=0 EndX=0 EndY=30.5 EndZ=0
    g16: LineSegment StartX=-3.5 StartY=5 StartZ=0 EndX=0 EndY=5 EndZ=0
  constraints (33):
    c: Weight(g0) = 1
    c: Equal(g0,g1)
    c: Equal(g0,g2)
    c: InternalAlignment(g0,g3)
    c: InternalAlignment(g1,g3)
    c: InternalAlignment(g2,g3)
    c: InternalAlignment(g4,g3)
    c: InternalAlignment(g5,g3)
    c: Block(g3)
    c: Weight(g6) = 1
    c: Equal(g6,g7)
    c: Equal(g6,g8)
    c: InternalAlignment(g6,g9)
    c: InternalAlignment(g7,g9)
    c: InternalAlignment(g8,g9)
    c: InternalAlignment(g10,g9)
    c: InternalAlignment(g11,g9)
    c: Block(g9)
    c: Coincident(g12,g9)
    c: Coincident(g12,g3)
    c: Vertical(g12)
    c: Coincident(g13,g9)
    c: Horizontal(g13)
    c: Distance(g13) = 4.8
    c: Coincident(g14,g3)
    c: Vertical(g14)
    c: Coincident(g15,g13)
    c: Vertical(g15)
    c: Tangent(g15,g1)
    c: Distance(g14) = 2
    c: Coincident(g16,g14)
    c: Horizontal(g16)
    c: Coincident(g15,g16)
FEATURE [Part::Feature] Face050
  shape: bbox 4.8 x 25.5 x 2e-07 mm, 1 faces, 0 solids (baked)
FEATURE [Part::Revolution] Revolve054  label="moreFrontCaseScrewPost001"
  Angle = 360
  Axis = (0,1,0)
  Base = (0,0,0)
  FaceMakerClass = Part::FaceMakerBullseye
  Placement = pos=(102.5,4.5,3.5) rot=(0,0,1;0rad)
  Solid = false
  Source = -> Face050
  Symmetric = false
FEATURE [Part::Feature] Face051
  shape: bbox 4.8 x 25.5 x 2e-07 mm, 1 faces, 0 solids (baked)
FEATURE [Part::Revolution] Revolve055  label="moreFrontCaseScrewPost002"
  Angle = 360
  Axis = (0,1,0)
  Base = (0,0,0)
  FaceMakerClass = Part::FaceMakerBullseye
  Placement = pos=(102.5,4.5,68.5) rot=(0,0,1;0rad)
  Solid = false
  Source = -> Face051
  Symmetric = false
FEATURE [Sketcher::SketchObject] Sketch027
  FullyConstrained = true
  sketch-geometry (10):
    g0: LineSegment StartX=-1.6 StartY=4.7 StartZ=0 EndX=-1.6 EndY=1.7 EndZ=0
    g1: LineSegment StartX=-3.5 StartY=4.7 StartZ=0 EndX=-1.6 EndY=4.7 EndZ=0
    g2: LineSegment StartX=-1.6 StartY=1.7 StartZ=0 EndX=-1.6 EndY=1.5 EndZ=0
    g3: LineSegment StartX=-1.6 StartY=1.5 StartZ=0 EndX=-5.2 EndY=1.5 EndZ=0
    g4: Circle CenterX=-3.5 CenterY=4.7 CenterZ=0 NormalX=0 NormalY=0 NormalZ=1 AngleXU=0 Radius=1
    g5: Circle CenterX=-3.59627 CenterY=2.99743 CenterZ=0 NormalX=0 NormalY=0 NormalZ=1 AngleXU=0 Radius=1
    g6: Circle CenterX=-5.2 CenterY=1.5 CenterZ=0 NormalX=0 NormalY=0 NormalZ=1 AngleXU=0 Radius=1
    g7: BSplineCurve PolesCount=3 KnotsCount=2 Degree=2 IsPeriodic=0
    g8: GeomPoint X=-3.5 Y=4.7 Z=0
    g9: GeomPoint X=-5.2 Y=1.5 Z=0
  constraints (23):
    c: Vertical(g0)
    c: Distance(g0) = 3
    c: Coincident(g1,g0)
    c: Horizontal(g1)
    c: Block(g0)
    c: Block(g1)
    c: Coincident(g2,g0)
    c: Vertical(g2)
    c: Distance(g2) = 0.2
    c: Coincident(g3,g2)
    c: Horizontal(g3)
    c: Block(g3)
    c: Coincident(g7,g1)
    c: Weight(g4) = 1
    c: Equal(g4,g5)
    c: Equal(g4,g6)
    c: Coincident(g7,g3)
    c: InternalAlignment(g4,g7)
    c: InternalAlignment(g5,g7)
    c: InternalAlignment(g6,g7)
    c: InternalAlignment(g8,g7)
    c: InternalAlignment(g9,g7)
    c: Block(g7)
FEATURE [Sketcher::SketchObject] Sketch028
  FullyConstrained = true
  sketch-geometry (18):
    g0: LineSegment StartX=0 StartY=3e-16 StartZ=0 EndX=0 EndY=1.7 EndZ=0
    g1: LineSegment StartX=-3.5 StartY=0 StartZ=0 EndX=-3.5 EndY=0.9 EndZ=0
    g2: Circle CenterX=-2.7 CenterY=1.7 CenterZ=0 NormalX=0 NormalY=0 NormalZ=1 AngleXU=0 Radius=1
    g3: Circle CenterX=-3.5 CenterY=1.7 CenterZ=0 NormalX=0 NormalY=0 NormalZ=1 AngleXU=0 Radius=1
    g4: Circle CenterX=-3.5 CenterY=0.9 CenterZ=0 NormalX=0 NormalY=0 NormalZ=1 AngleXU=0 Radius=1
    g5: BSplineCurve PolesCount=3 KnotsCount=2 Degree=2 IsPeriodic=0
    g6: GeomPoint X=-2.7 Y=1.7 Z=0
    g7: GeomPoint X=-3.5 Y=0.9 Z=0
    g8: LineSegment StartX=-3.5 StartY=0 StartZ=0 EndX=-3.5 EndY=-7 EndZ=0
    g9: LineSegment StartX=0 StartY=3e-16 StartZ=0 EndX=0 EndY=-7 EndZ=0
    g10: LineSegment StartX=-3.5 StartY=-7 StartZ=0 EndX=0 EndY=-7 EndZ=0
    g11: LineSegment StartX=-2.7 StartY=1.7 StartZ=0 EndX=-1.6 EndY=1.7 EndZ=0
    g12: LineSegment StartX=0 StartY=1.7 StartZ=0 EndX=0 EndY=4.5 EndZ=0
    g13: LineSegment StartX=0 StartY=4.5 StartZ=0 EndX=0 EndY=10.8 EndZ=0
    g14: LineSegment StartX=0 StartY=10.8 StartZ=0 EndX=-2 EndY=10.8 EndZ=0
    g15: LineSegment StartX=-1.6 StartY=4.7 StartZ=0 EndX=-1.6 EndY=1.7 EndZ=0
    g16: LineSegment StartX=-1.6 StartY=4.7 StartZ=0 EndX=-2 EndY=4.7 EndZ=0
    g17: LineSegment StartX=-2 StartY=4.7 StartZ=0 EndX=-2 EndY=10.8 EndZ=0
  constraints (44):
    c: Vertical(g0)
    c: Vertical(g1)
    c: Distance(g1) = 0.9
    c: Block(g0)
    c: Distance(g0) = 1.7
    c: Weight(g2) = 1
    c: Equal(g2,g3)
    c: Equal(g2,g4)
    c: Coincident(g5,g1)
    c: InternalAlignment(g2,g5)
    c: InternalAlignment(g3,g5)
    c: InternalAlignment(g4,g5)
    c: InternalAlignment(g6,g5)
    c: InternalAlignment(g7,g5)
    c: Block(g5)
    c: Coincident(g8,g1)
    c: Vertical(g8)
    c: Distance(g8) = 7
    c: Vertical(g9)
    c: Equal(g8,g9) = 7
    c: Coincident(g9,g0)
    c: Coincident(g10,g8)
    c: Coincident(g10,g9)
    c: Horizontal(g10)
    c: Coincident(g11,g5)
    c: Horizontal(g11)
    c: Coincident(g12,g0)
    c: Vertical(g12)
    c: Distance(g12) = 2.8
    c: Coincident(g13,g12)
    c: Vertical(g13)
    c: Distance(g13) = 6.3
    c: Coincident(g14,g13)
    c: Horizontal(g14)
    c: Distance(g14) = 2
    c: Vertical(g15)
    c: Distance(g15) = 3
    c: Block(g11)
    c: Coincident(g15,g11)
    c: Coincident(g16,g15)
    c: Horizontal(g16)
    c: Coincident(g17,g16)
    c: Coincident(g17,g14)
    c: Vertical(g17)
FEATURE [Part::Revolution] Revolve040  label="backCaseScrewRetainer001"
  Angle = 360
  Axis = (0,1,0)
  Base = (0,0,0)
  FaceMakerClass = Part::FaceMakerBullseye
  Placement = pos=(12.5,3,10) rot=(0,0,1;0rad)
  Solid = false
  Source = -> Face036
  Symmetric = false
FEATURE [Part::Feature] Face055
  shape: bbox 3.5 x 30.2 x 2e-07 mm, 1 faces, 0 solids (baked)
FEATURE [Part::Revolution] Revolve059  label="backCaseScrewPost"
  Angle = 360
  Axis = (0,1,0)
  Base = (0,0,0)
  FaceMakerClass = Part::FaceMakerBullseye
  Placement = pos=(12.5,4.5,10) rot=(0,0,1;0rad)
  Solid = false
  Source = -> Face055
  Symmetric = false
FEATURE [Part::Feature] Face056
  shape: bbox 3.5 x 30.2 x 2e-07 mm, 1 faces, 0 solids (baked)
FEATURE [Part::Revolution] Revolve060  label="backCaseScrewPost001"
  Angle = 360
  Axis = (0,1,0)
  Base = (0,0,0)
  FaceMakerClass = Part::FaceMakerBullseye
  Placement = pos=(12.5,4.5,62) rot=(0,0,1;0rad)
  Solid = false
  Source = -> Face056
  Symmetric = false
FEATURE [Part::Feature] Face057
  shape: bbox 3.5 x 17.8 x 2e-07 mm, 1 faces, 0 solids (baked)
FEATURE [Part::Revolution] Revolve061  label="removeToCreateScrewAndThreadedInsertHole"
  Angle = 360
  Axis = (0,1,0)
  Base = (0,0,0)
  FaceMakerClass = Part::FaceMakerBullseye
  Placement = pos=(12.5,0,10) rot=(0,0,1;0rad)
  Solid = false
  Source = -> Face057
  Symmetric = false
FEATURE [Part::Feature] Face058
  shape: bbox 3.5 x 17.8 x 2e-07 mm, 1 faces, 0 solids (baked)
FEATURE [Part::Revolution] Revolve062  label="removeToCreateScrewAndThreadedInsertHole001"
  Angle = 360
  Axis = (0,1,0)
  Base = (0,0,0)
  FaceMakerClass = Part::FaceMakerBullseye
  Placement = pos=(12.5,0,62) rot=(0,0,1;0rad)
  Solid = false
  Source = -> Face058
  Symmetric = false
FEATURE [Part::Feature] Face059
  shape: bbox 3.5 x 17.8 x 2e-07 mm, 1 faces, 0 solids (baked)
FEATURE [Part::Revolution] Revolve063  label="removeToCreateScrewAndThreadedInsertHole002"
  Angle = 360
  Axis = (0,1,0)
  Base = (0,0,0)
  FaceMakerClass = Part::FaceMakerBullseye
  Placement = pos=(89.5,0,68.5) rot=(0,0,1;0rad)
  Solid = false
  Source = -> Face059
  Symmetric = false
FEATURE [Part::Feature] Face060
  shape: bbox 3.5 x 17.8 x 2e-07 mm, 1 faces, 0 solids (baked)
FEATURE [Part::Revolution] Revolve064  label="removeToCreateScrewAndThreadedInsertHole003"
  Angle = 360
  Axis = (0,1,0)
  Base = (0,0,0)
  FaceMakerClass = Part::FaceMakerBullseye
  Placement = pos=(89.5,0,3.5) rot=(0,0,1;0rad)
  Solid = false
  Source = -> Face060
  Symmetric = false
FEATURE [Part::Feature] Face061
  shape: bbox 3.5 x 17.8 x 2e-07 mm, 1 faces, 0 solids (baked)
FEATURE [Part::Revolution] Revolve065  label="removeToCreateScrewAndThreadedInsertHole004"
  Angle = 360
  Axis = (0,1,0)
  Base = (0,0,0)
  FaceMakerClass = Part::FaceMakerBullseye
  Placement = pos=(102.5,4.7,3.5) rot=(0,0,1;0rad)
  Solid = false
  Source = -> Face061
  Symmetric = false
FEATURE [Part::Feature] Face062
  shape: bbox 3.5 x 17.8 x 2e-07 mm, 1 faces, 0 solids (baked)
FEATURE [Part::Revolution] Revolve066  label="removeToCreateScrewAndThreadedInsertHole005"
  Angle = 360
  Axis = (0,1,0)
  Base = (0,0,0)
  FaceMakerClass = Part::FaceMakerBullseye
  Placement = pos=(102.5,4.7,68.5) rot=(0,0,1;0rad)
  Solid = false
  Source = -> Face062
  Symmetric = false
FEATURE [Part::MultiFuse] Fusion047  label="makeHoles"
  Shapes = -> [Revolve066,Revolve065,Revolve064,Revolve063,Revolve062,Revolve061]
FEATURE [Part::Feature] Face063
  shape: bbox 3.6 x 3.2 x 2e-07 mm, 1 faces, 0 solids (baked)
FEATURE [Part::Revolution] Revolve067  label="moreFrontCaseScrewRetainer002"
  Angle = 360
  Axis = (0,1,0)
  Base = (0,0,0)
  FaceMakerClass = Part::FaceMakerBullseye
  Placement = pos=(102.5,4.5,68.5) rot=(0,0,1;0rad)
  Solid = false
  Source = -> Face063
  Symmetric = false
FEATURE [Part::Feature] Face064
  shape: bbox 3.6 x 3.2 x 2e-07 mm, 1 faces, 0 solids (baked)
FEATURE [Part::Revolution] Revolve068  label="moreFrontCaseScrewRetainer003"
  Angle = 360
  Axis = (0,1,0)
  Base = (0,0,0)
  FaceMakerClass = Part::FaceMakerBullseye
  Placement = pos=(102.5,4.5,3.5) rot=(0,0,1;0rad)
  Solid = false
  Source = -> Face064
  Symmetric = false
FEATURE [Part::Cut] Cut014  label="bottom003"
  Base = -> Cut007
  Tool = -> Fusion047
FEATURE [Part::Feature] Face065
  shape: bbox 3.5 x 17.8 x 2e-07 mm, 1 faces, 0 solids (baked)
FEATURE [Part::Revolution] Revolve069  label="removeToCreateScrewAndThreadedInsertHole006"
  Angle = 360
  Axis = (0,1,0)
  Base = (0,0,0)
  FaceMakerClass = Part::FaceMakerBullseye
  Placement = pos=(12.5,0,10) rot=(0,0,1;0rad)
  Solid = false
  Source = -> Face065
  Symmetric = false
FEATURE [Part::Feature] Face066
  shape: bbox 3.5 x 17.8 x 2e-07 mm, 1 faces, 0 solids (baked)
FEATURE [Part::Revolution] Revolve070  label="removeToCreateScrewAndThreadedInsertHole007"
  Angle = 360
  Axis = (0,1,0)
  Base = (0,0,0)
  FaceMakerClass = Part::FaceMakerBullseye
  Placement = pos=(12.5,0,62) rot=(0,0,1;0rad)
  Solid = false
  Source = -> Face066
  Symmetric = false
FEATURE [Part::Feature] Face067
  shape: bbox 3.5 x 17.8 x 2e-07 mm, 1 faces, 0 solids (baked)
FEATURE [Part::Revolution] Revolve071  label="removeToCreateScrewAndThreadedInsertHole008"
  Angle = 360
  Axis = (0,1,0)
  Base = (0,0,0)
  FaceMakerClass = Part::FaceMakerBullseye
  Placement = pos=(89.5,0,68.5) rot=(0,0,1;0rad)
  Solid = false
  Source = -> Face067
  Symmetric = false
FEATURE [Part::Feature] Face068
  shape: bbox 3.5 x 17.8 x 2e-07 mm, 1 faces, 0 solids (baked)
FEATURE [Part::Revolution] Revolve072  label="removeToCreateScrewAndThreadedInsertHole009"
  Angle = 360
  Axis = (0,1,0)
  Base = (0,0,0)
  FaceMakerClass = Part::FaceMakerBullseye
  Placement = pos=(89.5,0,3.5) rot=(0,0,1;0rad)
  Solid = false
  Source = -> Face068
  Symmetric = false
FEATURE [Part::Feature] Face069
  shape: bbox 3.5 x 17.8 x 2e-07 mm, 1 faces, 0 solids (baked)
FEATURE [Part::Feature] Face070
  shape: bbox 3.5 x 17.8 x 2e-07 mm, 1 faces, 0 solids (baked)
FEATURE [Part::Revolution] Revolve073  label="removeToCreateScrewAndThreadedInsertHole010"
  Angle = 360
  Axis = (0,1,0)
  Base = (0,0,0)
  FaceMakerClass = Part::FaceMakerBullseye
  Placement = pos=(102.5,4.7,3.5) rot=(0,0,1;0rad)
  Solid = false
  Source = -> Face069
  Symmetric = false
FEATURE [Part::Revolution] Revolve074  label="removeToCreateScrewAndThreadedInsertHole011"
  Angle = 360
  Axis = (0,1,0)
  Base = (0,0,0)
  FaceMakerClass = Part::FaceMakerBullseye
  Placement = pos=(102.5,4.7,68.5) rot=(0,0,1;0rad)
  Solid = false
  Source = -> Face070
  Symmetric = false
FEATURE [Part::MultiFuse] Fusion048  label="makeHoles001"
  Shapes = -> [Revolve074,Revolve073,Revolve072,Revolve071,Revolve070,Revolve069]
FEATURE [Part::MultiFuse] Fusion049  label="caseScrewRetainers"
  Shapes = -> [Revolve067,Revolve068,Revolve048,Revolve047,Revolve039,Revolve040]
FEATURE [Part::Cut] Cut015  label="caseScrewRetainers001"
  Base = -> Fusion049
  Tool = -> Fusion048
FEATURE [Part::MultiFuse] Fusion050  label="casePillars"
  Shapes = -> [Revolve055,Revolve054,Revolve043,Revolve046,Revolve059,Revolve060]
FEATURE [Part::Feature] Face071 .. Face076  x6 (patterned run collapsed; names and placements below)
  shape: bbox 3.5 x 17.8 x 2e-07 mm, 1 faces, 0 solids (baked)
FEATURE [Part::Revolution] Revolve075  label="removeToCreateScrewAndThreadedInsertHole012"
  Angle = 360
  Axis = (0,1,0)
  Base = (0,0,0)
  FaceMakerClass = Part::FaceMakerBullseye
  Placement = pos=(12.5,0,10) rot=(0,0,1;0rad)
  Solid = false
  Source = -> Face071
  Symmetric = false
FEATURE [Part::Revolution] Revolve076  label="removeToCreateScrewAndThreadedInsertHole013"
  Angle = 360
  Axis = (0,1,0)
  Base = (0,0,0)
  FaceMakerClass = Part::FaceMakerBullseye
  Placement = pos=(12.5,0,62) rot=(0,0,1;0rad)
  Solid = false
  Source = -> Face072
  Symmetric = false
FEATURE [Part::Revolution] Revolve077  label="removeToCreateScrewAndThreadedInsertHole014"
  Angle = 360
  Axis = (0,1,0)
  Base = (0,0,0)
  FaceMakerClass = Part::FaceMakerBullseye
  Placement = pos=(89.5,0,68.5) rot=(0,0,1;0rad)
  Solid = false
  Source = -> Face073
  Symmetric = false
FEATURE [Part::Revolution] Revolve078  label="removeToCreateScrewAndThreadedInsertHole015"
  Angle = 360
  Axis = (0,1,0)
  Base = (0,0,0)
  FaceMakerClass = Part::FaceMakerBullseye
  Placement = pos=(89.5,0,3.5) rot=(0,0,1;0rad)
  Solid = false
  Source = -> Face074
  Symmetric = false
FEATURE [Part::Revolution] Revolve079  label="removeToCreateScrewAndThreadedInsertHole016"
  Angle = 360
  Axis = (0,1,0)
  Base = (0,0,0)
  FaceMakerClass = Part::FaceMakerBullseye
  Placement = pos=(102.5,4.7,3.5) rot=(0,0,1;0rad)
  Solid = false
  Source = -> Face075
  Symmetric = false
FEATURE [Part::Revolution] Revolve080  label="removeToCreateScrewAndThreadedInsertHole017"
  Angle = 360
  Axis = (0,1,0)
  Base = (0,0,0)
  FaceMakerClass = Part::FaceMakerBullseye
  Placement = pos=(102.5,4.7,68.5) rot=(0,0,1;0rad)
  Solid = false
  Source = -> Face076
  Symmetric = false
FEATURE [Part::MultiFuse] Fusion051  label="makeHoles002"
  Shapes = -> [Revolve080,Revolve079,Revolve078,Revolve077,Revolve076,Revolve075]
FEATURE [Part::Cut] Cut016  label="caesPillars"
  Base = -> Fusion050
  Tool = -> Fusion051
FEATURE [Part::Revolution] Revolve009  label="plugHousing016"
  Angle = 360
  Axis = (0,1,0)
  Base = (0,0,0)
  FaceMakerClass = Part::FaceMakerBullseye
  Placement = pos=(0,0,36.15) rot=(0,0,1;0rad)
  Solid = false
  Source = -> Face012
  Symmetric = false
FEATURE [Part::MultiFuse] Fusion014  label="plugHousing023"
  Placement = pos=(0,0,0) rot=(0,0,1;1.5708rad)
  Shapes = -> [Revolve011,Revolve009]
FEATURE [Part::Revolution] Revolve010  label="plugHousing017"
  Angle = 360
  Axis = (0,1,0)
  Base = (0,0,0)
  FaceMakerClass = Part::FaceMakerBullseye
  Placement = pos=(0,0,36.15) rot=(0,0,1;0rad)
  Solid = false
  Source = -> Face014
  Symmetric = false
FEATURE [Part::MultiFuse] Fusion015  label="plugHousing024"
  Placement = pos=(0,0,0) rot=(0,0,1;1.5708rad)
  Shapes = -> [Revolve010,Revolve015]
FEATURE [Part::Revolution] Revolve014  label="plugHousing026"
  Angle = 360
  Axis = (0,1,0)
  Base = (0,0,0)
  FaceMakerClass = Part::FaceMakerBullseye
  Placement = pos=(0,0,36.15) rot=(0,0,1;0rad)
  Solid = false
  Source = -> Face011
  Symmetric = false
FEATURE [Part::Revolution] Revolve013  label="plugHousing025"
  Angle = 360
  Axis = (0,1,0)
  Base = (0,0,0)
  FaceMakerClass = Part::FaceMakerBullseye
  Placement = pos=(0,0,36.15) rot=(0,0,1;0rad)
  Solid = false
  Source = -> Face015
  Symmetric = false
FEATURE [Part::MultiFuse] Fusion016  label="plugHousing028"
  Placement = pos=(0,19,0) rot=(0,0,1;3.14159rad)
  Shapes = -> [Fusion014,Fusion013]
FEATURE [Part::MultiFuse] Fusion011  label="plugHousing018"
  Placement = pos=(0,0,0) rot=(0,0,1;1.5708rad)
  Shapes = -> [Revolve014,Revolve013]
FEATURE [Part::MultiFuse] Fusion012  label="plugHousing019"
  Placement = pos=(0,19,0) rot=(0,0,1;3.14159rad)
  Shapes = -> [Fusion011,Fusion015]
FEATURE [Part::MultiFuse] Fusion017  label="plugHousing029"
  Placement = pos=(122.621,0,-0.15) rot=(0,0,1;0rad)
  Shapes = -> [Fusion016,Fusion012]
FEATURE [Part::MultiFuse] Fusion052  label="casePillarRetainers"
  Shapes = -> [Extrude012,Extrude013,Extrude014,Extrude015,Extrude016,Extrude017,Extrude018,Extrude019,Box011,Box012]
FEATURE [Part::Feature] Face077
  shape: bbox 3.5 x 17.8 x 2e-07 mm, 1 faces, 0 solids (baked)
FEATURE [Part::Revolution] Revolve081  label="removeToCreateScrewAndThreadedInsertHole018"
  Angle = 360
  Axis = (0,1,0)
  Base = (0,0,0)
  FaceMakerClass = Part::FaceMakerBullseye
  Placement = pos=(62.3,30.3,19.7) rot=(0,0,1;0rad)
  Solid = false
  Source = -> Face077
  Symmetric = false
FEATURE [Part::Feature] Face078
  shape: bbox 3.5 x 17.8 x 2e-07 mm, 1 faces, 0 solids (baked)
FEATURE [Part::Revolution] Revolve082  label="removeToCreateScrewAndThreadedInsertHole019"
  Angle = 360
  Axis = (0,1,0)
  Base = (0,0,0)
  FaceMakerClass = Part::FaceMakerBullseye
  Placement = pos=(62.3,30.3,51.7) rot=(0,0,1;0rad)
  Solid = false
  Source = -> Face078
  Symmetric = false
FEATURE [Part::Feature] Face079
  shape: bbox 3.5 x 17.8 x 2e-07 mm, 1 faces, 0 solids (baked)
FEATURE [Part::Revolution] Revolve083  label="removeToCreateScrewAndThreadedInsertHole020"
  Angle = 360
  Axis = (0,1,0)
  Base = (0,0,0)
  FaceMakerClass = Part::FaceMakerBullseye
  Placement = pos=(30.3,30.3,19.7) rot=(0,0,1;0rad)
  Solid = false
  Source = -> Face079
  Symmetric = false
FEATURE [Part::Feature] Face080
  shape: bbox 3.5 x 17.8 x 2e-07 mm, 1 faces, 0 solids (baked)
FEATURE [Part::Revolution] Revolve084  label="removeToCreateScrewAndThreadedInsertHole021"
  Angle = 360
  Axis = (0,1,0)
  Base = (0,0,0)
  FaceMakerClass = Part::FaceMakerBullseye
  Placement = pos=(30.3,30.3,51.7) rot=(0,0,1;0rad)
  Solid = false
  Source = -> Face080
  Symmetric = false
